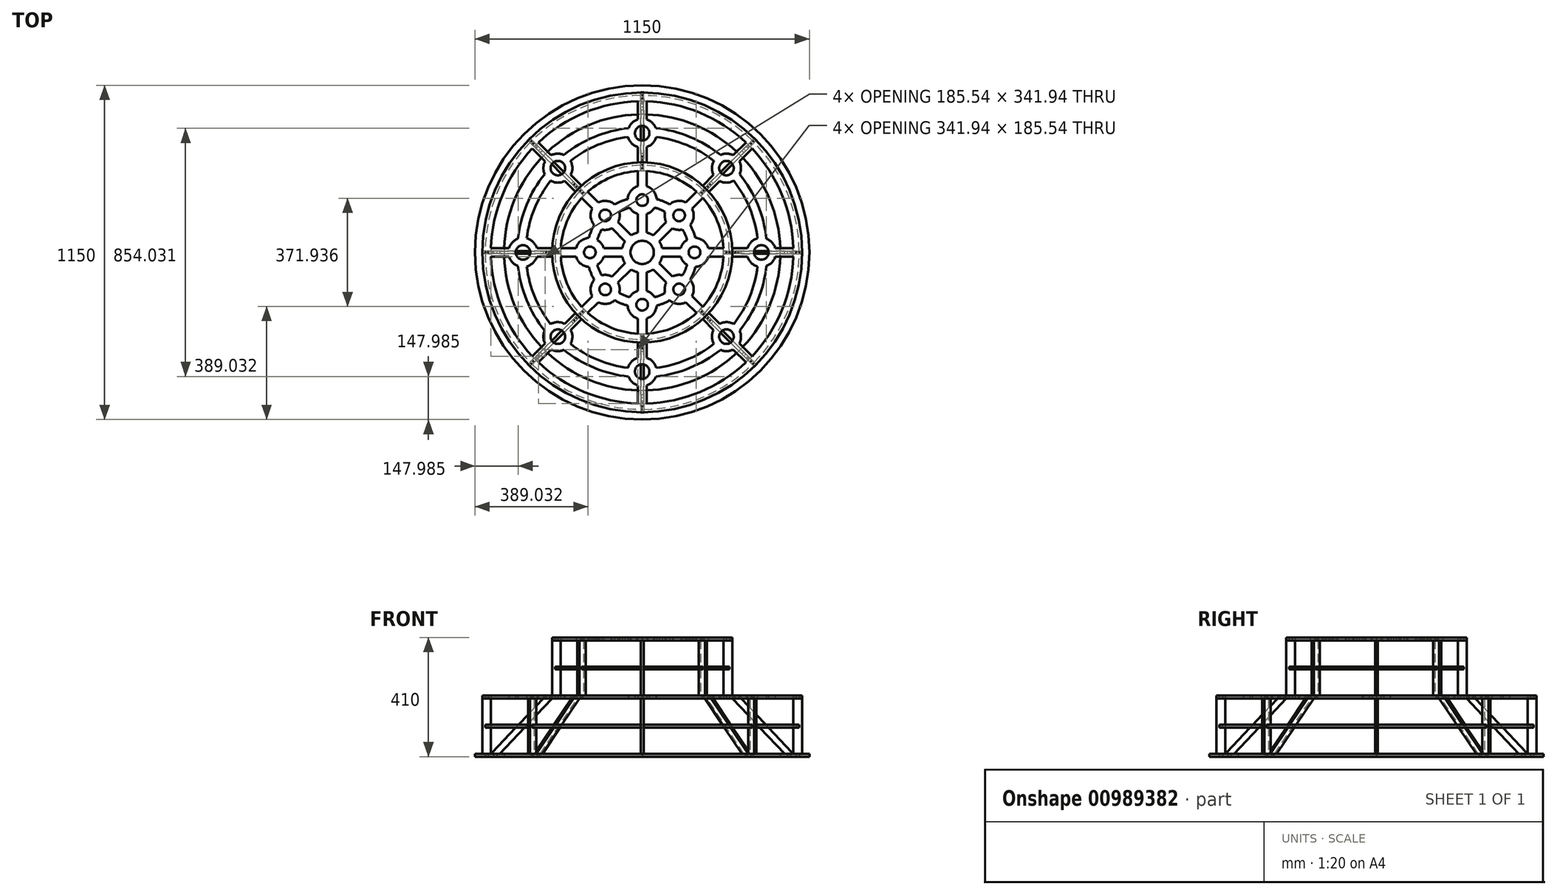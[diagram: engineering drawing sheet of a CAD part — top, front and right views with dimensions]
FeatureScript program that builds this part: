
annotation { "Feature Type Name" : "Feature", "Feature Type Description" : "" }
export const myFeature = defineFeature(function(context is Context, id is Id, definition is map)
    precondition{}
    {
        {
            var Q0;
            Q0=qCreatedBy(makeId("Top.planeOp"),FACE);
            cPlane(context, id + "F0", {"entities" : qUnion([Q0]), "cplaneType" : CPlaneType.OFFSET, "offset" : 200 * mm, "width" : 150 * mm, "height" : 150 * mm});
        }
        {
            var Q0;
            Q0=qCreatedBy(makeId("Top.planeOp"),FACE);
            cPlane(context, id + "F1", {"entities" : qUnion([Q0]), "cplaneType" : CPlaneType.OFFSET, "offset" : 200 * mm, "oppositeDirection" : true, "width" : 150 * mm, "height" : 150 * mm});
        }
        {
            var Q0;
            Q0=qCreatedBy(makeId("Top.planeOp"),FACE);
            cPlane(context, id + "F2", {"entities" : qUnion([Q0]), "cplaneType" : CPlaneType.OFFSET, "offset" : 100 * mm, "oppositeDirection" : true, "width" : 150 * mm, "height" : 150 * mm});
        }
        {
            var Q0;
            Q0=qCreatedBy(makeId("Top.planeOp"),FACE);
            cPlane(context, id + "F3", {"entities" : qUnion([Q0]), "cplaneType" : CPlaneType.OFFSET, "offset" : 100 * mm, "width" : 150 * mm, "height" : 150 * mm});
        }
        {
            var Q0;
            Q0=qCreatedBy(makeId("Top.planeOp"),FACE);
            var sketch = newSketch(context, id + "F4", { "sketchPlane" : qUnion([Q0])});
            skCircle(sketch, "E0", {"center": v(0, 0) * mm, "radius": 550 * mm});
            skArc(sketch, "E1", {"start": v(15, -519.78) * mm, "mid": v(199, -480.42) * mm, "end": v(356.94, -378.15) * mm});
            skArc(sketch, "E2", {"start": v(46.86, -427.44) * mm, "mid": v(164.55, -397.27) * mm, "end": v(269.1, -335.38) * mm});
            skArc(sketch, "E3", {"start": v(48.3, -397.07) * mm, "mid": v(153.07, -369.55) * mm, "end": v(246.62, -314.93) * mm});
            skArc(sketch, "E4", {"start": v(15, -309.64) * mm, "mid": v(118.63, -286.4) * mm, "end": v(208.34, -229.55) * mm});
            skCircle(sketch, "E5", {"center": v(0, 0) * mm, "radius": 280 * mm});
            skCircle(sketch, "E6", {"center": v(0, 0) * mm, "radius": 190 * mm, "construction": true});
            skCircle(sketch, "E7", {"center": v(0, 0) * mm, "radius": 160 * mm, "construction": true});
            skCircle(sketch, "E8", {"center": v(0, 0) * mm, "radius": 40 * mm, "construction": true});
            skCircle(sketch, "E9", {"center": v(0, 0) * mm, "radius": 70 * mm, "construction": true});
            skLineSegment(sketch, "E10", {"start": v(0, 725.48) * mm, "end": v(0, -722.46) * mm, "construction": true});
            skLineSegment(sketch, "E11", {"start": v(-695.44, 0) * mm, "end": v(901.66, 0) * mm, "construction": true});
            skArc(sketch, "E12", {"start": v(-15, -362.3) * mm, "mid": v(-36.11, -375.42) * mm, "end": v(-48.3, -397.07) * mm});
            skCircle(sketch, "E13", {"center": v(0, -410) * mm, "radius": 25 * mm});
            skLineSegment(sketch, "E14", {"start": v(15, -519.78) * mm, "end": v(15, -457.7) * mm});
            skLineSegment(sketch, "E15", {"start": v(-15, -457.7) * mm, "end": v(-15, -519.78) * mm});
            skLineSegment(sketch, "E16", {"start": v(-15, -362.3) * mm, "end": v(-15, -309.64) * mm});
            skLineSegment(sketch, "E17", {"start": v(15, -362.3) * mm, "end": v(15, -309.64) * mm});
            skArc(sketch, "E18.trimOffspring", {"start": v(-46.86, -427.44) * mm, "mid": v(-34.43, -446.26) * mm, "end": v(-15, -457.7) * mm});
            skArc(sketch, "E19.trimOffspring", {"start": v(48.3, -397.07) * mm, "mid": v(36.11, -375.42) * mm, "end": v(15, -362.3) * mm});
            skArc(sketch, "E20.trimOffspring", {"start": v(15, -457.7) * mm, "mid": v(34.43, -446.26) * mm, "end": v(46.86, -427.44) * mm});
            skArc(sketch, "E21.1.0", {"start": v(334.25, -313.03) * mm, "mid": v(339.9, -291.2) * mm, "end": v(335.38, -269.1) * mm});
            skCircle(sketch, "E21.1.1", {"center": v(289.91, -289.91) * mm, "radius": 25 * mm});
            skLineSegment(sketch, "E21.1.2", {"start": v(266.8, -245.58) * mm, "end": v(229.55, -208.34) * mm});
            skLineSegment(sketch, "E21.1.3", {"start": v(245.58, -266.8) * mm, "end": v(208.34, -229.55) * mm});
            skArc(sketch, "E21.1.4", {"start": v(245.58, -266.8) * mm, "mid": v(239.93, -291) * mm, "end": v(246.62, -314.93) * mm});
            skArc(sketch, "E21.1.5", {"start": v(269.1, -335.38) * mm, "mid": v(291.2, -339.9) * mm, "end": v(313.03, -334.25) * mm});
            skArc(sketch, "E21.1.6", {"start": v(314.93, -246.62) * mm, "mid": v(291, -239.93) * mm, "end": v(266.8, -245.58) * mm});
            skLineSegment(sketch, "E21.1.7", {"start": v(378.15, -356.94) * mm, "end": v(334.25, -313.03) * mm});
            skLineSegment(sketch, "E21.1.8", {"start": v(313.03, -334.25) * mm, "end": v(356.94, -378.15) * mm});
            skArc(sketch, "E21.2.0", {"start": v(457.7, 15) * mm, "mid": v(446.26, 34.43) * mm, "end": v(427.44, 46.86) * mm});
            skCircle(sketch, "E21.2.1", {"center": v(410, 0) * mm, "radius": 25 * mm});
            skLineSegment(sketch, "E21.2.2", {"start": v(362.3, 15) * mm, "end": v(309.64, 15) * mm});
            skLineSegment(sketch, "E21.2.3", {"start": v(362.3, -15) * mm, "end": v(309.64, -15) * mm});
            skArc(sketch, "E21.2.4", {"start": v(362.3, -15) * mm, "mid": v(375.42, -36.11) * mm, "end": v(397.07, -48.3) * mm});
            skArc(sketch, "E21.2.5", {"start": v(427.44, -46.86) * mm, "mid": v(446.26, -34.43) * mm, "end": v(457.7, -15) * mm});
            skArc(sketch, "E21.2.6", {"start": v(397.07, 48.3) * mm, "mid": v(375.42, 36.11) * mm, "end": v(362.3, 15) * mm});
            skLineSegment(sketch, "E21.2.7", {"start": v(519.78, 15) * mm, "end": v(457.7, 15) * mm});
            skLineSegment(sketch, "E21.2.8", {"start": v(457.7, -15) * mm, "end": v(519.78, -15) * mm});
            skArc(sketch, "E21.3.0", {"start": v(313.03, 334.25) * mm, "mid": v(291.2, 339.9) * mm, "end": v(269.1, 335.38) * mm});
            skCircle(sketch, "E21.3.1", {"center": v(289.91, 289.91) * mm, "radius": 25 * mm});
            skLineSegment(sketch, "E21.3.2", {"start": v(245.58, 266.8) * mm, "end": v(208.34, 229.55) * mm});
            skLineSegment(sketch, "E21.3.3", {"start": v(266.8, 245.58) * mm, "end": v(229.55, 208.34) * mm});
            skArc(sketch, "E21.3.4", {"start": v(266.8, 245.58) * mm, "mid": v(291, 239.93) * mm, "end": v(314.93, 246.62) * mm});
            skArc(sketch, "E21.3.5", {"start": v(335.38, 269.1) * mm, "mid": v(339.9, 291.2) * mm, "end": v(334.25, 313.03) * mm});
            skArc(sketch, "E21.3.6", {"start": v(246.62, 314.93) * mm, "mid": v(239.93, 291) * mm, "end": v(245.58, 266.8) * mm});
            skLineSegment(sketch, "E21.3.7", {"start": v(356.94, 378.15) * mm, "end": v(313.03, 334.25) * mm});
            skLineSegment(sketch, "E21.3.8", {"start": v(334.25, 313.03) * mm, "end": v(378.15, 356.94) * mm});
            skArc(sketch, "E21.4.0", {"start": v(-15, 457.7) * mm, "mid": v(-34.43, 446.26) * mm, "end": v(-46.86, 427.44) * mm});
            skCircle(sketch, "E21.4.1", {"center": v(0, 410) * mm, "radius": 25 * mm});
            skLineSegment(sketch, "E21.4.2", {"start": v(-15, 362.3) * mm, "end": v(-15, 309.64) * mm});
            skLineSegment(sketch, "E21.4.3", {"start": v(15, 362.3) * mm, "end": v(15, 309.64) * mm});
            skArc(sketch, "E21.4.4", {"start": v(15, 362.3) * mm, "mid": v(36.11, 375.42) * mm, "end": v(48.3, 397.07) * mm});
            skArc(sketch, "E21.4.5", {"start": v(46.86, 427.44) * mm, "mid": v(34.43, 446.26) * mm, "end": v(15, 457.7) * mm});
            skArc(sketch, "E21.4.6", {"start": v(-48.3, 397.07) * mm, "mid": v(-36.11, 375.42) * mm, "end": v(-15, 362.3) * mm});
            skLineSegment(sketch, "E21.4.7", {"start": v(-15, 519.78) * mm, "end": v(-15, 457.7) * mm});
            skLineSegment(sketch, "E21.4.8", {"start": v(15, 457.7) * mm, "end": v(15, 519.78) * mm});
            skArc(sketch, "E21.5.0", {"start": v(-334.25, 313.03) * mm, "mid": v(-339.9, 291.2) * mm, "end": v(-335.38, 269.1) * mm});
            skCircle(sketch, "E21.5.1", {"center": v(-289.91, 289.91) * mm, "radius": 25 * mm});
            skLineSegment(sketch, "E21.5.2", {"start": v(-266.8, 245.58) * mm, "end": v(-229.55, 208.34) * mm});
            skLineSegment(sketch, "E21.5.3", {"start": v(-245.58, 266.8) * mm, "end": v(-208.34, 229.55) * mm});
            skArc(sketch, "E21.5.4", {"start": v(-245.58, 266.8) * mm, "mid": v(-239.93, 291) * mm, "end": v(-246.62, 314.93) * mm});
            skArc(sketch, "E21.5.5", {"start": v(-269.1, 335.38) * mm, "mid": v(-291.2, 339.9) * mm, "end": v(-313.03, 334.25) * mm});
            skArc(sketch, "E21.5.6", {"start": v(-314.93, 246.62) * mm, "mid": v(-291, 239.93) * mm, "end": v(-266.8, 245.58) * mm});
            skLineSegment(sketch, "E21.5.7", {"start": v(-378.15, 356.94) * mm, "end": v(-334.25, 313.03) * mm});
            skLineSegment(sketch, "E21.5.8", {"start": v(-313.03, 334.25) * mm, "end": v(-356.94, 378.15) * mm});
            skArc(sketch, "E21.6.0", {"start": v(-457.7, -15) * mm, "mid": v(-446.26, -34.43) * mm, "end": v(-427.44, -46.86) * mm});
            skCircle(sketch, "E21.6.1", {"center": v(-410, 0) * mm, "radius": 25 * mm});
            skLineSegment(sketch, "E21.6.2", {"start": v(-362.3, -15) * mm, "end": v(-309.64, -15) * mm});
            skLineSegment(sketch, "E21.6.3", {"start": v(-362.3, 15) * mm, "end": v(-309.64, 15) * mm});
            skArc(sketch, "E21.6.4", {"start": v(-362.3, 15) * mm, "mid": v(-375.42, 36.11) * mm, "end": v(-397.07, 48.3) * mm});
            skArc(sketch, "E21.6.5", {"start": v(-427.44, 46.86) * mm, "mid": v(-446.26, 34.43) * mm, "end": v(-457.7, 15) * mm});
            skArc(sketch, "E21.6.6", {"start": v(-397.07, -48.3) * mm, "mid": v(-375.42, -36.11) * mm, "end": v(-362.3, -15) * mm});
            skLineSegment(sketch, "E21.6.7", {"start": v(-519.78, -15) * mm, "end": v(-457.7, -15) * mm});
            skLineSegment(sketch, "E21.6.8", {"start": v(-457.7, 15) * mm, "end": v(-519.78, 15) * mm});
            skArc(sketch, "E21.7.0", {"start": v(-313.03, -334.25) * mm, "mid": v(-291.2, -339.9) * mm, "end": v(-269.1, -335.38) * mm});
            skCircle(sketch, "E21.7.1", {"center": v(-289.91, -289.91) * mm, "radius": 25 * mm});
            skLineSegment(sketch, "E21.7.2", {"start": v(-245.58, -266.8) * mm, "end": v(-208.34, -229.55) * mm});
            skLineSegment(sketch, "E21.7.3", {"start": v(-266.8, -245.58) * mm, "end": v(-229.55, -208.34) * mm});
            skArc(sketch, "E21.7.4", {"start": v(-266.8, -245.58) * mm, "mid": v(-291, -239.93) * mm, "end": v(-314.93, -246.62) * mm});
            skArc(sketch, "E21.7.5", {"start": v(-335.38, -269.1) * mm, "mid": v(-339.9, -291.2) * mm, "end": v(-334.25, -313.03) * mm});
            skArc(sketch, "E21.7.6", {"start": v(-246.62, -314.93) * mm, "mid": v(-239.93, -291) * mm, "end": v(-245.58, -266.8) * mm});
            skLineSegment(sketch, "E21.7.7", {"start": v(-356.94, -378.15) * mm, "end": v(-313.03, -334.25) * mm});
            skLineSegment(sketch, "E21.7.8", {"start": v(-334.25, -313.03) * mm, "end": v(-378.15, -356.94) * mm});
            skArc(sketch, "E22.trimOffspring", {"start": v(-246.62, -314.93) * mm, "mid": v(-153.07, -369.55) * mm, "end": v(-48.3, -397.07) * mm});
            skArc(sketch, "E23.trimOffspring", {"start": v(-269.1, -335.38) * mm, "mid": v(-164.55, -397.27) * mm, "end": v(-46.86, -427.44) * mm});
            skArc(sketch, "E24.trimOffspring", {"start": v(-356.94, -378.15) * mm, "mid": v(-199, -480.42) * mm, "end": v(-15, -519.78) * mm});
            skArc(sketch, "E25.trimOffspring", {"start": v(-208.34, -229.55) * mm, "mid": v(-118.63, -286.4) * mm, "end": v(-15, -309.64) * mm});
            skArc(sketch, "E26.trimOffspring", {"start": v(-397.07, -48.3) * mm, "mid": v(-369.55, -153.07) * mm, "end": v(-314.93, -246.62) * mm});
            skArc(sketch, "E27.trimOffspring", {"start": v(-427.44, -46.86) * mm, "mid": v(-397.27, -164.55) * mm, "end": v(-335.38, -269.1) * mm});
            skArc(sketch, "E28.trimOffspring", {"start": v(-309.64, -15) * mm, "mid": v(-286.4, -118.63) * mm, "end": v(-229.55, -208.34) * mm});
            skArc(sketch, "E29.trimOffspring", {"start": v(-519.78, -15) * mm, "mid": v(-480.42, -199) * mm, "end": v(-378.15, -356.94) * mm});
            skArc(sketch, "E30.trimOffspring", {"start": v(-314.93, 246.62) * mm, "mid": v(-369.55, 153.07) * mm, "end": v(-397.07, 48.3) * mm});
            skArc(sketch, "E31.trimOffspring", {"start": v(-335.38, 269.1) * mm, "mid": v(-397.27, 164.55) * mm, "end": v(-427.44, 46.86) * mm});
            skArc(sketch, "E32.trimOffspring", {"start": v(-378.15, 356.94) * mm, "mid": v(-480.42, 199) * mm, "end": v(-519.78, 15) * mm});
            skArc(sketch, "E33.trimOffspring", {"start": v(-229.55, 208.34) * mm, "mid": v(-286.4, 118.63) * mm, "end": v(-309.64, 15) * mm});
            skArc(sketch, "E34.trimOffspring", {"start": v(-15, 309.64) * mm, "mid": v(-118.63, 286.4) * mm, "end": v(-208.34, 229.55) * mm});
            skArc(sketch, "E35.trimOffspring", {"start": v(-48.3, 397.07) * mm, "mid": v(-153.07, 369.55) * mm, "end": v(-246.62, 314.93) * mm});
            skArc(sketch, "E36.trimOffspring", {"start": v(-46.86, 427.44) * mm, "mid": v(-164.55, 397.27) * mm, "end": v(-269.1, 335.38) * mm});
            skArc(sketch, "E37.trimOffspring", {"start": v(-15, 519.78) * mm, "mid": v(-199, 480.42) * mm, "end": v(-356.94, 378.15) * mm});
            skArc(sketch, "E38.trimOffspring", {"start": v(269.1, 335.38) * mm, "mid": v(164.55, 397.27) * mm, "end": v(46.86, 427.44) * mm});
            skArc(sketch, "E39.trimOffspring", {"start": v(246.62, 314.93) * mm, "mid": v(153.07, 369.55) * mm, "end": v(48.3, 397.07) * mm});
            skArc(sketch, "E40.trimOffspring", {"start": v(208.34, 229.55) * mm, "mid": v(118.63, 286.4) * mm, "end": v(15, 309.64) * mm});
            skArc(sketch, "E41.trimOffspring", {"start": v(356.94, 378.15) * mm, "mid": v(199, 480.42) * mm, "end": v(15, 519.78) * mm});
            skArc(sketch, "E42.trimOffspring", {"start": v(309.64, 15) * mm, "mid": v(286.4, 118.63) * mm, "end": v(229.55, 208.34) * mm});
            skArc(sketch, "E43.trimOffspring", {"start": v(397.07, 48.3) * mm, "mid": v(369.55, 153.07) * mm, "end": v(314.93, 246.62) * mm});
            skArc(sketch, "E44.trimOffspring", {"start": v(427.44, 46.86) * mm, "mid": v(397.27, 164.55) * mm, "end": v(335.38, 269.1) * mm});
            skArc(sketch, "E45.trimOffspring", {"start": v(519.78, 15) * mm, "mid": v(480.42, 199) * mm, "end": v(378.15, 356.94) * mm});
            skArc(sketch, "E46.trimOffspring", {"start": v(335.38, -269.1) * mm, "mid": v(397.27, -164.55) * mm, "end": v(427.44, -46.86) * mm});
            skArc(sketch, "E47.trimOffspring", {"start": v(314.93, -246.62) * mm, "mid": v(369.55, -153.07) * mm, "end": v(397.07, -48.3) * mm});
            skArc(sketch, "E48.trimOffspring", {"start": v(378.15, -356.94) * mm, "mid": v(480.42, -199) * mm, "end": v(519.78, -15) * mm});
            skArc(sketch, "E49.trimOffspring", {"start": v(229.55, -208.34) * mm, "mid": v(286.4, -118.63) * mm, "end": v(309.64, -15) * mm});
            skLineSegment(sketch, "E50.bottom", {"start": v(4.9, 530) * mm, "end": v(1, 530) * mm});
            skLineSegment(sketch, "E50.top", {"start": v(4.9, 540) * mm, "end": v(1, 540) * mm});
            skLineSegment(sketch, "E50.left", {"start": v(4.9, 530) * mm, "end": v(4.9, 540) * mm});
            skLineSegment(sketch, "E50.right", {"start": v(-4.9, 530) * mm, "end": v(-4.9, 540) * mm});
            skPoint(sketch, "E50.middle", {"position": v(0, 535) * mm});
            skLineSegment(sketch, "E51", {"start": v(0, 541) * mm, "end": v(-1, 540) * mm});
            skLineSegment(sketch, "E52", {"start": v(0, 541) * mm, "end": v(1, 540) * mm});
            skLineSegment(sketch, "E53.trimOffspring", {"start": v(-1, 540) * mm, "end": v(-4.9, 540) * mm});
            skLineSegment(sketch, "E54", {"start": v(0, 529) * mm, "end": v(-1, 530) * mm});
            skLineSegment(sketch, "E55", {"start": v(0, 529) * mm, "end": v(1, 530) * mm});
            skLineSegment(sketch, "E56.trimOffspring", {"start": v(-1, 530) * mm, "end": v(-4.9, 530) * mm});
            skPoint(sketch, "E57.1.0", {"position": v(-378.3, 378.3) * mm});
            skLineSegment(sketch, "E57.1.1", {"start": v(-378.23, 371.3) * mm, "end": v(-385.3, 378.37) * mm});
            skLineSegment(sketch, "E57.1.2", {"start": v(-371.3, 378.23) * mm, "end": v(-378.37, 385.3) * mm});
            skLineSegment(sketch, "E57.1.3", {"start": v(-371.3, 378.23) * mm, "end": v(-374.06, 375.47) * mm});
            skLineSegment(sketch, "E57.1.4", {"start": v(-374.06, 374.06) * mm, "end": v(-374.06, 375.47) * mm});
            skLineSegment(sketch, "E57.1.5", {"start": v(-374.06, 374.06) * mm, "end": v(-375.47, 374.06) * mm});
            skLineSegment(sketch, "E57.1.6", {"start": v(-375.47, 374.06) * mm, "end": v(-378.23, 371.3) * mm});
            skLineSegment(sketch, "E57.1.7", {"start": v(-378.37, 385.3) * mm, "end": v(-381.13, 382.54) * mm});
            skLineSegment(sketch, "E57.1.8", {"start": v(-382.54, 381.13) * mm, "end": v(-385.3, 378.37) * mm});
            skLineSegment(sketch, "E57.1.9", {"start": v(-382.54, 382.54) * mm, "end": v(-381.13, 382.54) * mm});
            skLineSegment(sketch, "E57.1.10", {"start": v(-382.54, 382.54) * mm, "end": v(-382.54, 381.13) * mm});
            skPoint(sketch, "E57.2.0", {"position": v(-535, 0) * mm});
            skLineSegment(sketch, "E57.2.1", {"start": v(-530, -4.9) * mm, "end": v(-540, -4.9) * mm});
            skLineSegment(sketch, "E57.2.2", {"start": v(-530, 4.9) * mm, "end": v(-540, 4.9) * mm});
            skLineSegment(sketch, "E57.2.3", {"start": v(-530, 4.9) * mm, "end": v(-530, 1) * mm});
            skLineSegment(sketch, "E57.2.4", {"start": v(-529, 0) * mm, "end": v(-530, 1) * mm});
            skLineSegment(sketch, "E57.2.5", {"start": v(-529, 0) * mm, "end": v(-530, -1) * mm});
            skLineSegment(sketch, "E57.2.6", {"start": v(-530, -1) * mm, "end": v(-530, -4.9) * mm});
            skLineSegment(sketch, "E57.2.7", {"start": v(-540, 4.9) * mm, "end": v(-540, 1) * mm});
            skLineSegment(sketch, "E57.2.8", {"start": v(-540, -1) * mm, "end": v(-540, -4.9) * mm});
            skLineSegment(sketch, "E57.2.9", {"start": v(-541, 0) * mm, "end": v(-540, 1) * mm});
            skLineSegment(sketch, "E57.2.10", {"start": v(-541, 0) * mm, "end": v(-540, -1) * mm});
            skPoint(sketch, "E57.3.0", {"position": v(-378.3, -378.3) * mm});
            skLineSegment(sketch, "E57.3.1", {"start": v(-371.3, -378.23) * mm, "end": v(-378.37, -385.3) * mm});
            skLineSegment(sketch, "E57.3.2", {"start": v(-378.23, -371.3) * mm, "end": v(-385.3, -378.37) * mm});
            skLineSegment(sketch, "E57.3.3", {"start": v(-378.23, -371.3) * mm, "end": v(-375.47, -374.06) * mm});
            skLineSegment(sketch, "E57.3.4", {"start": v(-374.06, -374.06) * mm, "end": v(-375.47, -374.06) * mm});
            skLineSegment(sketch, "E57.3.5", {"start": v(-374.06, -374.06) * mm, "end": v(-374.06, -375.47) * mm});
            skLineSegment(sketch, "E57.3.6", {"start": v(-374.06, -375.47) * mm, "end": v(-371.3, -378.23) * mm});
            skLineSegment(sketch, "E57.3.7", {"start": v(-385.3, -378.37) * mm, "end": v(-382.54, -381.13) * mm});
            skLineSegment(sketch, "E57.3.8", {"start": v(-381.13, -382.54) * mm, "end": v(-378.37, -385.3) * mm});
            skLineSegment(sketch, "E57.3.9", {"start": v(-382.54, -382.54) * mm, "end": v(-382.54, -381.13) * mm});
            skLineSegment(sketch, "E57.3.10", {"start": v(-382.54, -382.54) * mm, "end": v(-381.13, -382.54) * mm});
            skPoint(sketch, "E57.4.0", {"position": v(0, -535) * mm});
            skLineSegment(sketch, "E57.4.1", {"start": v(4.9, -530) * mm, "end": v(4.9, -540) * mm});
            skLineSegment(sketch, "E57.4.2", {"start": v(-4.9, -530) * mm, "end": v(-4.9, -540) * mm});
            skLineSegment(sketch, "E57.4.3", {"start": v(-4.9, -530) * mm, "end": v(-1, -530) * mm});
            skLineSegment(sketch, "E57.4.4", {"start": v(0, -529) * mm, "end": v(-1, -530) * mm});
            skLineSegment(sketch, "E57.4.5", {"start": v(0, -529) * mm, "end": v(1, -530) * mm});
            skLineSegment(sketch, "E57.4.6", {"start": v(1, -530) * mm, "end": v(4.9, -530) * mm});
            skLineSegment(sketch, "E57.4.7", {"start": v(-4.9, -540) * mm, "end": v(-1, -540) * mm});
            skLineSegment(sketch, "E57.4.8", {"start": v(1, -540) * mm, "end": v(4.9, -540) * mm});
            skLineSegment(sketch, "E57.4.9", {"start": v(0, -541) * mm, "end": v(-1, -540) * mm});
            skLineSegment(sketch, "E57.4.10", {"start": v(0, -541) * mm, "end": v(1, -540) * mm});
            skPoint(sketch, "E57.5.0", {"position": v(378.3, -378.3) * mm});
            skLineSegment(sketch, "E57.5.1", {"start": v(378.23, -371.3) * mm, "end": v(385.3, -378.37) * mm});
            skLineSegment(sketch, "E57.5.2", {"start": v(371.3, -378.23) * mm, "end": v(378.37, -385.3) * mm});
            skLineSegment(sketch, "E57.5.3", {"start": v(371.3, -378.23) * mm, "end": v(374.06, -375.47) * mm});
            skLineSegment(sketch, "E57.5.4", {"start": v(374.06, -374.06) * mm, "end": v(374.06, -375.47) * mm});
            skLineSegment(sketch, "E57.5.5", {"start": v(374.06, -374.06) * mm, "end": v(375.47, -374.06) * mm});
            skLineSegment(sketch, "E57.5.6", {"start": v(375.47, -374.06) * mm, "end": v(378.23, -371.3) * mm});
            skLineSegment(sketch, "E57.5.7", {"start": v(378.37, -385.3) * mm, "end": v(381.13, -382.54) * mm});
            skLineSegment(sketch, "E57.5.8", {"start": v(382.54, -381.13) * mm, "end": v(385.3, -378.37) * mm});
            skLineSegment(sketch, "E57.5.9", {"start": v(382.54, -382.54) * mm, "end": v(381.13, -382.54) * mm});
            skLineSegment(sketch, "E57.5.10", {"start": v(382.54, -382.54) * mm, "end": v(382.54, -381.13) * mm});
            skPoint(sketch, "E57.6.0", {"position": v(535, 0) * mm});
            skLineSegment(sketch, "E57.6.1", {"start": v(530, 4.9) * mm, "end": v(540, 4.9) * mm});
            skLineSegment(sketch, "E57.6.2", {"start": v(530, -4.9) * mm, "end": v(540, -4.9) * mm});
            skLineSegment(sketch, "E57.6.3", {"start": v(530, -4.9) * mm, "end": v(530, -1) * mm});
            skLineSegment(sketch, "E57.6.4", {"start": v(529, 0) * mm, "end": v(530, -1) * mm});
            skLineSegment(sketch, "E57.6.5", {"start": v(529, 0) * mm, "end": v(530, 1) * mm});
            skLineSegment(sketch, "E57.6.6", {"start": v(530, 1) * mm, "end": v(530, 4.9) * mm});
            skLineSegment(sketch, "E57.6.7", {"start": v(540, -4.9) * mm, "end": v(540, -1) * mm});
            skLineSegment(sketch, "E57.6.8", {"start": v(540, 1) * mm, "end": v(540, 4.9) * mm});
            skLineSegment(sketch, "E57.6.9", {"start": v(541, 0) * mm, "end": v(540, -1) * mm});
            skLineSegment(sketch, "E57.6.10", {"start": v(541, 0) * mm, "end": v(540, 1) * mm});
            skPoint(sketch, "E57.7.0", {"position": v(378.3, 378.3) * mm});
            skLineSegment(sketch, "E57.7.1", {"start": v(371.3, 378.23) * mm, "end": v(378.37, 385.3) * mm});
            skLineSegment(sketch, "E57.7.2", {"start": v(378.23, 371.3) * mm, "end": v(385.3, 378.37) * mm});
            skLineSegment(sketch, "E57.7.3", {"start": v(378.23, 371.3) * mm, "end": v(375.47, 374.06) * mm});
            skLineSegment(sketch, "E57.7.4", {"start": v(374.06, 374.06) * mm, "end": v(375.47, 374.06) * mm});
            skLineSegment(sketch, "E57.7.5", {"start": v(374.06, 374.06) * mm, "end": v(374.06, 375.47) * mm});
            skLineSegment(sketch, "E57.7.6", {"start": v(374.06, 375.47) * mm, "end": v(371.3, 378.23) * mm});
            skLineSegment(sketch, "E57.7.7", {"start": v(385.3, 378.37) * mm, "end": v(382.54, 381.13) * mm});
            skLineSegment(sketch, "E57.7.8", {"start": v(381.13, 382.54) * mm, "end": v(378.37, 385.3) * mm});
            skLineSegment(sketch, "E57.7.9", {"start": v(382.54, 382.54) * mm, "end": v(382.54, 381.13) * mm});
            skLineSegment(sketch, "E57.7.10", {"start": v(382.54, 382.54) * mm, "end": v(381.13, 382.54) * mm});
            skLineSegment(sketch, "E58.bottom", {"start": v(4.9, 290) * mm, "end": v(1, 290) * mm});
            skLineSegment(sketch, "E58.top", {"start": v(4.9, 300) * mm, "end": v(1, 300) * mm});
            skLineSegment(sketch, "E58.left", {"start": v(4.9, 290) * mm, "end": v(4.9, 300) * mm});
            skLineSegment(sketch, "E58.right", {"start": v(-4.9, 290) * mm, "end": v(-4.9, 300) * mm});
            skPoint(sketch, "E58.middle", {"position": v(0, 295) * mm});
            skLineSegment(sketch, "E59", {"start": v(0, 301) * mm, "end": v(-1, 300) * mm});
            skLineSegment(sketch, "E60", {"start": v(0, 301) * mm, "end": v(1, 300) * mm});
            skLineSegment(sketch, "E61.trimOffspring", {"start": v(-1, 300) * mm, "end": v(-4.9, 300) * mm});
            skLineSegment(sketch, "E62", {"start": v(0, 289) * mm, "end": v(-1, 290) * mm});
            skLineSegment(sketch, "E63", {"start": v(0, 289) * mm, "end": v(1, 290) * mm});
            skLineSegment(sketch, "E64.trimOffspring", {"start": v(-1, 290) * mm, "end": v(-4.9, 290) * mm});
            skLineSegment(sketch, "E65.1.0", {"start": v(-201.6, 208.53) * mm, "end": v(-208.67, 215.6) * mm});
            skPoint(sketch, "E65.1.1", {"position": v(-208.6, 208.6) * mm});
            skLineSegment(sketch, "E65.1.2", {"start": v(-208.53, 201.6) * mm, "end": v(-215.6, 208.67) * mm});
            skLineSegment(sketch, "E65.1.3", {"start": v(-205.77, 204.35) * mm, "end": v(-208.53, 201.6) * mm});
            skLineSegment(sketch, "E65.1.4", {"start": v(-208.67, 215.6) * mm, "end": v(-211.42, 212.84) * mm});
            skLineSegment(sketch, "E65.1.5", {"start": v(-201.6, 208.53) * mm, "end": v(-204.35, 205.77) * mm});
            skLineSegment(sketch, "E65.1.6", {"start": v(-212.84, 211.42) * mm, "end": v(-215.6, 208.67) * mm});
            skLineSegment(sketch, "E65.1.7", {"start": v(-204.35, 204.35) * mm, "end": v(-205.77, 204.35) * mm});
            skLineSegment(sketch, "E65.1.8", {"start": v(-212.84, 212.84) * mm, "end": v(-211.42, 212.84) * mm});
            skLineSegment(sketch, "E65.1.9", {"start": v(-212.84, 212.84) * mm, "end": v(-212.84, 211.42) * mm});
            skLineSegment(sketch, "E65.1.10", {"start": v(-204.35, 204.35) * mm, "end": v(-204.35, 205.77) * mm});
            skLineSegment(sketch, "E65.2.0", {"start": v(-290, 4.9) * mm, "end": v(-300, 4.9) * mm});
            skPoint(sketch, "E65.2.1", {"position": v(-295, 0) * mm});
            skLineSegment(sketch, "E65.2.2", {"start": v(-290, -4.9) * mm, "end": v(-300, -4.9) * mm});
            skLineSegment(sketch, "E65.2.3", {"start": v(-290, -1) * mm, "end": v(-290, -4.9) * mm});
            skLineSegment(sketch, "E65.2.4", {"start": v(-300, 4.9) * mm, "end": v(-300, 1) * mm});
            skLineSegment(sketch, "E65.2.5", {"start": v(-290, 4.9) * mm, "end": v(-290, 1) * mm});
            skLineSegment(sketch, "E65.2.6", {"start": v(-300, -1) * mm, "end": v(-300, -4.9) * mm});
            skLineSegment(sketch, "E65.2.7", {"start": v(-289, 0) * mm, "end": v(-290, -1) * mm});
            skLineSegment(sketch, "E65.2.8", {"start": v(-301, 0) * mm, "end": v(-300, 1) * mm});
            skLineSegment(sketch, "E65.2.9", {"start": v(-301, 0) * mm, "end": v(-300, -1) * mm});
            skLineSegment(sketch, "E65.2.10", {"start": v(-289, 0) * mm, "end": v(-290, 1) * mm});
            skLineSegment(sketch, "E65.3.0", {"start": v(-208.53, -201.6) * mm, "end": v(-215.6, -208.67) * mm});
            skPoint(sketch, "E65.3.1", {"position": v(-208.6, -208.6) * mm});
            skLineSegment(sketch, "E65.3.2", {"start": v(-201.6, -208.53) * mm, "end": v(-208.67, -215.6) * mm});
            skLineSegment(sketch, "E65.3.3", {"start": v(-204.35, -205.77) * mm, "end": v(-201.6, -208.53) * mm});
            skLineSegment(sketch, "E65.3.4", {"start": v(-215.6, -208.67) * mm, "end": v(-212.84, -211.42) * mm});
            skLineSegment(sketch, "E65.3.5", {"start": v(-208.53, -201.6) * mm, "end": v(-205.77, -204.35) * mm});
            skLineSegment(sketch, "E65.3.6", {"start": v(-211.42, -212.84) * mm, "end": v(-208.67, -215.6) * mm});
            skLineSegment(sketch, "E65.3.7", {"start": v(-204.35, -204.35) * mm, "end": v(-204.35, -205.77) * mm});
            skLineSegment(sketch, "E65.3.8", {"start": v(-212.84, -212.84) * mm, "end": v(-212.84, -211.42) * mm});
            skLineSegment(sketch, "E65.3.9", {"start": v(-212.84, -212.84) * mm, "end": v(-211.42, -212.84) * mm});
            skLineSegment(sketch, "E65.3.10", {"start": v(-204.35, -204.35) * mm, "end": v(-205.77, -204.35) * mm});
            skLineSegment(sketch, "E65.4.0", {"start": v(-4.9, -290) * mm, "end": v(-4.9, -300) * mm});
            skPoint(sketch, "E65.4.1", {"position": v(0, -295) * mm});
            skLineSegment(sketch, "E65.4.2", {"start": v(4.9, -290) * mm, "end": v(4.9, -300) * mm});
            skLineSegment(sketch, "E65.4.3", {"start": v(1, -290) * mm, "end": v(4.9, -290) * mm});
            skLineSegment(sketch, "E65.4.4", {"start": v(-4.9, -300) * mm, "end": v(-1, -300) * mm});
            skLineSegment(sketch, "E65.4.5", {"start": v(-4.9, -290) * mm, "end": v(-1, -290) * mm});
            skLineSegment(sketch, "E65.4.6", {"start": v(1, -300) * mm, "end": v(4.9, -300) * mm});
            skLineSegment(sketch, "E65.4.7", {"start": v(0, -289) * mm, "end": v(1, -290) * mm});
            skLineSegment(sketch, "E65.4.8", {"start": v(0, -301) * mm, "end": v(-1, -300) * mm});
            skLineSegment(sketch, "E65.4.9", {"start": v(0, -301) * mm, "end": v(1, -300) * mm});
            skLineSegment(sketch, "E65.4.10", {"start": v(0, -289) * mm, "end": v(-1, -290) * mm});
            skLineSegment(sketch, "E65.5.0", {"start": v(201.6, -208.53) * mm, "end": v(208.67, -215.6) * mm});
            skPoint(sketch, "E65.5.1", {"position": v(208.6, -208.6) * mm});
            skLineSegment(sketch, "E65.5.2", {"start": v(208.53, -201.6) * mm, "end": v(215.6, -208.67) * mm});
            skLineSegment(sketch, "E65.5.3", {"start": v(205.77, -204.35) * mm, "end": v(208.53, -201.6) * mm});
            skLineSegment(sketch, "E65.5.4", {"start": v(208.67, -215.6) * mm, "end": v(211.42, -212.84) * mm});
            skLineSegment(sketch, "E65.5.5", {"start": v(201.6, -208.53) * mm, "end": v(204.35, -205.77) * mm});
            skLineSegment(sketch, "E65.5.6", {"start": v(212.84, -211.42) * mm, "end": v(215.6, -208.67) * mm});
            skLineSegment(sketch, "E65.5.7", {"start": v(204.35, -204.35) * mm, "end": v(205.77, -204.35) * mm});
            skLineSegment(sketch, "E65.5.8", {"start": v(212.84, -212.84) * mm, "end": v(211.42, -212.84) * mm});
            skLineSegment(sketch, "E65.5.9", {"start": v(212.84, -212.84) * mm, "end": v(212.84, -211.42) * mm});
            skLineSegment(sketch, "E65.5.10", {"start": v(204.35, -204.35) * mm, "end": v(204.35, -205.77) * mm});
            skLineSegment(sketch, "E65.6.0", {"start": v(290, -4.9) * mm, "end": v(300, -4.9) * mm});
            skPoint(sketch, "E65.6.1", {"position": v(295, 0) * mm});
            skLineSegment(sketch, "E65.6.2", {"start": v(290, 4.9) * mm, "end": v(300, 4.9) * mm});
            skLineSegment(sketch, "E65.6.3", {"start": v(290, 1) * mm, "end": v(290, 4.9) * mm});
            skLineSegment(sketch, "E65.6.4", {"start": v(300, -4.9) * mm, "end": v(300, -1) * mm});
            skLineSegment(sketch, "E65.6.5", {"start": v(290, -4.9) * mm, "end": v(290, -1) * mm});
            skLineSegment(sketch, "E65.6.6", {"start": v(300, 1) * mm, "end": v(300, 4.9) * mm});
            skLineSegment(sketch, "E65.6.7", {"start": v(289, 0) * mm, "end": v(290, 1) * mm});
            skLineSegment(sketch, "E65.6.8", {"start": v(301, 0) * mm, "end": v(300, -1) * mm});
            skLineSegment(sketch, "E65.6.9", {"start": v(301, 0) * mm, "end": v(300, 1) * mm});
            skLineSegment(sketch, "E65.6.10", {"start": v(289, 0) * mm, "end": v(290, -1) * mm});
            skLineSegment(sketch, "E65.7.0", {"start": v(208.53, 201.6) * mm, "end": v(215.6, 208.67) * mm});
            skPoint(sketch, "E65.7.1", {"position": v(208.6, 208.6) * mm});
            skLineSegment(sketch, "E65.7.2", {"start": v(201.6, 208.53) * mm, "end": v(208.67, 215.6) * mm});
            skLineSegment(sketch, "E65.7.3", {"start": v(204.35, 205.77) * mm, "end": v(201.6, 208.53) * mm});
            skLineSegment(sketch, "E65.7.4", {"start": v(215.6, 208.67) * mm, "end": v(212.84, 211.42) * mm});
            skLineSegment(sketch, "E65.7.5", {"start": v(208.53, 201.6) * mm, "end": v(205.77, 204.35) * mm});
            skLineSegment(sketch, "E65.7.6", {"start": v(211.42, 212.84) * mm, "end": v(208.67, 215.6) * mm});
            skLineSegment(sketch, "E65.7.7", {"start": v(204.35, 204.35) * mm, "end": v(204.35, 205.77) * mm});
            skLineSegment(sketch, "E65.7.8", {"start": v(212.84, 212.84) * mm, "end": v(212.84, 211.42) * mm});
            skLineSegment(sketch, "E65.7.9", {"start": v(212.84, 212.84) * mm, "end": v(211.42, 212.84) * mm});
            skLineSegment(sketch, "E65.7.10", {"start": v(204.35, 204.35) * mm, "end": v(205.77, 204.35) * mm});
            skLineSegment(sketch, "E66.bottom", {"start": v(4.9, 320) * mm, "end": v(1, 320) * mm});
            skLineSegment(sketch, "E66.top", {"start": v(4.9, 330) * mm, "end": v(1, 330) * mm});
            skLineSegment(sketch, "E66.left", {"start": v(4.9, 320) * mm, "end": v(4.9, 330) * mm});
            skLineSegment(sketch, "E66.right", {"start": v(-4.9, 320) * mm, "end": v(-4.9, 330) * mm});
            skPoint(sketch, "E66.middle", {"position": v(0, 325) * mm});
            skLineSegment(sketch, "E67", {"start": v(0, 331) * mm, "end": v(-1, 330) * mm});
            skLineSegment(sketch, "E68", {"start": v(0, 331) * mm, "end": v(1, 330) * mm});
            skLineSegment(sketch, "E69.trimOffspring", {"start": v(-1, 330) * mm, "end": v(-4.9, 330) * mm});
            skLineSegment(sketch, "E70", {"start": v(0, 319) * mm, "end": v(-1, 320) * mm});
            skLineSegment(sketch, "E71", {"start": v(0, 319) * mm, "end": v(1, 320) * mm});
            skLineSegment(sketch, "E72.trimOffspring", {"start": v(-1, 320) * mm, "end": v(-4.9, 320) * mm});
            skLineSegment(sketch, "E73.1.0", {"start": v(-222.8, 229.74) * mm, "end": v(-225.57, 226.98) * mm});
            skLineSegment(sketch, "E73.1.1", {"start": v(-229.74, 222.8) * mm, "end": v(-236.81, 229.88) * mm});
            skLineSegment(sketch, "E73.1.2", {"start": v(-222.8, 229.74) * mm, "end": v(-229.88, 236.81) * mm});
            skLineSegment(sketch, "E73.1.3", {"start": v(-229.88, 236.81) * mm, "end": v(-232.64, 234.05) * mm});
            skLineSegment(sketch, "E73.1.4", {"start": v(-234.05, 232.64) * mm, "end": v(-236.81, 229.88) * mm});
            skLineSegment(sketch, "E73.1.5", {"start": v(-226.98, 225.57) * mm, "end": v(-229.74, 222.8) * mm});
            skPoint(sketch, "E73.1.6", {"position": v(-229.8, 229.8) * mm});
            skLineSegment(sketch, "E73.1.7", {"start": v(-225.57, 225.57) * mm, "end": v(-225.57, 226.98) * mm});
            skLineSegment(sketch, "E73.1.8", {"start": v(-225.57, 225.57) * mm, "end": v(-226.98, 225.57) * mm});
            skLineSegment(sketch, "E73.1.9", {"start": v(-234.05, 234.05) * mm, "end": v(-234.05, 232.64) * mm});
            skLineSegment(sketch, "E73.1.10", {"start": v(-234.05, 234.05) * mm, "end": v(-232.64, 234.05) * mm});
            skLineSegment(sketch, "E73.2.0", {"start": v(-320, 4.9) * mm, "end": v(-320, 1) * mm});
            skLineSegment(sketch, "E73.2.1", {"start": v(-320, -4.9) * mm, "end": v(-330, -4.9) * mm});
            skLineSegment(sketch, "E73.2.2", {"start": v(-320, 4.9) * mm, "end": v(-330, 4.9) * mm});
            skLineSegment(sketch, "E73.2.3", {"start": v(-330, 4.9) * mm, "end": v(-330, 1) * mm});
            skLineSegment(sketch, "E73.2.4", {"start": v(-330, -1) * mm, "end": v(-330, -4.9) * mm});
            skLineSegment(sketch, "E73.2.5", {"start": v(-320, -1) * mm, "end": v(-320, -4.9) * mm});
            skPoint(sketch, "E73.2.6", {"position": v(-325, 0) * mm});
            skLineSegment(sketch, "E73.2.7", {"start": v(-319, 0) * mm, "end": v(-320, 1) * mm});
            skLineSegment(sketch, "E73.2.8", {"start": v(-319, 0) * mm, "end": v(-320, -1) * mm});
            skLineSegment(sketch, "E73.2.9", {"start": v(-331, 0) * mm, "end": v(-330, -1) * mm});
            skLineSegment(sketch, "E73.2.10", {"start": v(-331, 0) * mm, "end": v(-330, 1) * mm});
            skLineSegment(sketch, "E73.3.0", {"start": v(-229.74, -222.8) * mm, "end": v(-226.98, -225.57) * mm});
            skLineSegment(sketch, "E73.3.1", {"start": v(-222.8, -229.74) * mm, "end": v(-229.88, -236.81) * mm});
            skLineSegment(sketch, "E73.3.2", {"start": v(-229.74, -222.8) * mm, "end": v(-236.81, -229.88) * mm});
            skLineSegment(sketch, "E73.3.3", {"start": v(-236.81, -229.88) * mm, "end": v(-234.05, -232.64) * mm});
            skLineSegment(sketch, "E73.3.4", {"start": v(-232.64, -234.05) * mm, "end": v(-229.88, -236.81) * mm});
            skLineSegment(sketch, "E73.3.5", {"start": v(-225.57, -226.98) * mm, "end": v(-222.8, -229.74) * mm});
            skPoint(sketch, "E73.3.6", {"position": v(-229.8, -229.8) * mm});
            skLineSegment(sketch, "E73.3.7", {"start": v(-225.57, -225.57) * mm, "end": v(-226.98, -225.57) * mm});
            skLineSegment(sketch, "E73.3.8", {"start": v(-225.57, -225.57) * mm, "end": v(-225.57, -226.98) * mm});
            skLineSegment(sketch, "E73.3.9", {"start": v(-234.05, -234.05) * mm, "end": v(-232.64, -234.05) * mm});
            skLineSegment(sketch, "E73.3.10", {"start": v(-234.05, -234.05) * mm, "end": v(-234.05, -232.64) * mm});
            skLineSegment(sketch, "E73.4.0", {"start": v(-4.9, -320) * mm, "end": v(-1, -320) * mm});
            skLineSegment(sketch, "E73.4.1", {"start": v(4.9, -320) * mm, "end": v(4.9, -330) * mm});
            skLineSegment(sketch, "E73.4.2", {"start": v(-4.9, -320) * mm, "end": v(-4.9, -330) * mm});
            skLineSegment(sketch, "E73.4.3", {"start": v(-4.9, -330) * mm, "end": v(-1, -330) * mm});
            skLineSegment(sketch, "E73.4.4", {"start": v(1, -330) * mm, "end": v(4.9, -330) * mm});
            skLineSegment(sketch, "E73.4.5", {"start": v(1, -320) * mm, "end": v(4.9, -320) * mm});
            skPoint(sketch, "E73.4.6", {"position": v(0, -325) * mm});
            skLineSegment(sketch, "E73.4.7", {"start": v(0, -319) * mm, "end": v(-1, -320) * mm});
            skLineSegment(sketch, "E73.4.8", {"start": v(0, -319) * mm, "end": v(1, -320) * mm});
            skLineSegment(sketch, "E73.4.9", {"start": v(0, -331) * mm, "end": v(1, -330) * mm});
            skLineSegment(sketch, "E73.4.10", {"start": v(0, -331) * mm, "end": v(-1, -330) * mm});
            skLineSegment(sketch, "E73.5.0", {"start": v(222.8, -229.74) * mm, "end": v(225.57, -226.98) * mm});
            skLineSegment(sketch, "E73.5.1", {"start": v(229.74, -222.8) * mm, "end": v(236.81, -229.88) * mm});
            skLineSegment(sketch, "E73.5.2", {"start": v(222.8, -229.74) * mm, "end": v(229.88, -236.81) * mm});
            skLineSegment(sketch, "E73.5.3", {"start": v(229.88, -236.81) * mm, "end": v(232.64, -234.05) * mm});
            skLineSegment(sketch, "E73.5.4", {"start": v(234.05, -232.64) * mm, "end": v(236.81, -229.88) * mm});
            skLineSegment(sketch, "E73.5.5", {"start": v(226.98, -225.57) * mm, "end": v(229.74, -222.8) * mm});
            skPoint(sketch, "E73.5.6", {"position": v(229.8, -229.8) * mm});
            skLineSegment(sketch, "E73.5.7", {"start": v(225.57, -225.57) * mm, "end": v(225.57, -226.98) * mm});
            skLineSegment(sketch, "E73.5.8", {"start": v(225.57, -225.57) * mm, "end": v(226.98, -225.57) * mm});
            skLineSegment(sketch, "E73.5.9", {"start": v(234.05, -234.05) * mm, "end": v(234.05, -232.64) * mm});
            skLineSegment(sketch, "E73.5.10", {"start": v(234.05, -234.05) * mm, "end": v(232.64, -234.05) * mm});
            skLineSegment(sketch, "E73.6.0", {"start": v(320, -4.9) * mm, "end": v(320, -1) * mm});
            skLineSegment(sketch, "E73.6.1", {"start": v(320, 4.9) * mm, "end": v(330, 4.9) * mm});
            skLineSegment(sketch, "E73.6.2", {"start": v(320, -4.9) * mm, "end": v(330, -4.9) * mm});
            skLineSegment(sketch, "E73.6.3", {"start": v(330, -4.9) * mm, "end": v(330, -1) * mm});
            skLineSegment(sketch, "E73.6.4", {"start": v(330, 1) * mm, "end": v(330, 4.9) * mm});
            skLineSegment(sketch, "E73.6.5", {"start": v(320, 1) * mm, "end": v(320, 4.9) * mm});
            skPoint(sketch, "E73.6.6", {"position": v(325, 0) * mm});
            skLineSegment(sketch, "E73.6.7", {"start": v(319, 0) * mm, "end": v(320, -1) * mm});
            skLineSegment(sketch, "E73.6.8", {"start": v(319, 0) * mm, "end": v(320, 1) * mm});
            skLineSegment(sketch, "E73.6.9", {"start": v(331, 0) * mm, "end": v(330, 1) * mm});
            skLineSegment(sketch, "E73.6.10", {"start": v(331, 0) * mm, "end": v(330, -1) * mm});
            skLineSegment(sketch, "E73.7.0", {"start": v(229.74, 222.8) * mm, "end": v(226.98, 225.57) * mm});
            skLineSegment(sketch, "E73.7.1", {"start": v(222.8, 229.74) * mm, "end": v(229.88, 236.81) * mm});
            skLineSegment(sketch, "E73.7.2", {"start": v(229.74, 222.8) * mm, "end": v(236.81, 229.88) * mm});
            skLineSegment(sketch, "E73.7.3", {"start": v(236.81, 229.88) * mm, "end": v(234.05, 232.64) * mm});
            skLineSegment(sketch, "E73.7.4", {"start": v(232.64, 234.05) * mm, "end": v(229.88, 236.81) * mm});
            skLineSegment(sketch, "E73.7.5", {"start": v(225.57, 226.98) * mm, "end": v(222.8, 229.74) * mm});
            skPoint(sketch, "E73.7.6", {"position": v(229.8, 229.8) * mm});
            skLineSegment(sketch, "E73.7.7", {"start": v(225.57, 225.57) * mm, "end": v(226.98, 225.57) * mm});
            skLineSegment(sketch, "E73.7.8", {"start": v(225.57, 225.57) * mm, "end": v(225.57, 226.98) * mm});
            skLineSegment(sketch, "E73.7.9", {"start": v(234.05, 234.05) * mm, "end": v(232.64, 234.05) * mm});
            skLineSegment(sketch, "E73.7.10", {"start": v(234.05, 234.05) * mm, "end": v(234.05, 232.64) * mm});
            skSolve(sketch);
        }
        {
            var Q0;
            Q0=qSketchRegion(id+"F4",true);
            extrude(context, id + "F5", {"entities" : qUnion([Q0]), "depth" : 10 * mm, "offsetDistance" : 25 * mm});
        }
        {
            var Q0;
            Q0=qCreatedBy(id+"F0.planeOp",FACE);
            var sketch = newSketch(context, id + "F6", { "sketchPlane" : qUnion([Q0])});
            skArc(sketch, "E74.0", {"start": v(42.8, -154.17) * mm, "mid": v(61.23, -147.82) * mm, "end": v(78.74, -139.28) * mm});
            skArc(sketch, "E75.0", {"start": v(49.89, -183.33) * mm, "mid": v(72.7, -175.54) * mm, "end": v(94.36, -164.91) * mm});
            skArc(sketch, "E76.0", {"start": v(15, -279.6) * mm, "mid": v(107.15, -258.69) * mm, "end": v(187.1, -208.31) * mm});
            skArc(sketch, "E77.0", {"start": v(15, -68.37) * mm, "mid": v(26.79, -64.67) * mm, "end": v(37.74, -58.95) * mm});
            skCircle(sketch, "E78.0", {"center": v(0, 0) * mm, "radius": 40 * mm});
            skPoint(sketch, "E79.0", {"position": v(15, 309.64) * mm});
            skCircle(sketch, "E80", {"center": v(0, 0) * mm, "radius": 310 * mm});
            skArc(sketch, "E81", {"start": v(-15, -132.3) * mm, "mid": v(-30.9, -140.7) * mm, "end": v(-42.8, -154.17) * mm});
            skCircle(sketch, "E82", {"center": v(0, -180) * mm, "radius": 20 * mm});
            skLineSegment(sketch, "E83", {"start": v(-15, -68.37) * mm, "end": v(-15, -132.3) * mm});
            skLineSegment(sketch, "E84", {"start": v(15, -68.37) * mm, "end": v(15, -132.3) * mm});
            skLineSegment(sketch, "E85", {"start": v(-15, -227.7) * mm, "end": v(-15, -279.6) * mm});
            skLineSegment(sketch, "E86", {"start": v(15, -227.7) * mm, "end": v(15, -279.6) * mm});
            skArc(sketch, "E87.trimOffspring", {"start": v(42.8, -154.17) * mm, "mid": v(30.9, -140.7) * mm, "end": v(15, -132.3) * mm});
            skArc(sketch, "E88.trimOffspring", {"start": v(15, -227.7) * mm, "mid": v(39.3, -210.9) * mm, "end": v(49.89, -183.33) * mm});
            skArc(sketch, "E89.trimOffspring", {"start": v(-49.89, -183.33) * mm, "mid": v(-39.3, -210.9) * mm, "end": v(-15, -227.7) * mm});
            skLineSegment(sketch, "E90.1.0", {"start": v(58.95, -37.74) * mm, "end": v(104.16, -82.95) * mm});
            skLineSegment(sketch, "E90.1.1", {"start": v(37.74, -58.95) * mm, "end": v(82.95, -104.16) * mm});
            skArc(sketch, "E90.1.2", {"start": v(82.95, -104.16) * mm, "mid": v(77.63, -121.34) * mm, "end": v(78.74, -139.28) * mm});
            skCircle(sketch, "E90.1.3", {"center": v(127.28, -127.28) * mm, "radius": 20 * mm});
            skArc(sketch, "E90.1.4", {"start": v(94.36, -164.91) * mm, "mid": v(121.34, -176.93) * mm, "end": v(150.4, -171.61) * mm});
            skArc(sketch, "E90.1.5", {"start": v(171.61, -150.4) * mm, "mid": v(176.93, -121.34) * mm, "end": v(164.91, -94.36) * mm});
            skArc(sketch, "E90.1.6", {"start": v(139.28, -78.74) * mm, "mid": v(121.34, -77.63) * mm, "end": v(104.16, -82.95) * mm});
            skLineSegment(sketch, "E90.1.7", {"start": v(171.61, -150.4) * mm, "end": v(208.31, -187.1) * mm});
            skLineSegment(sketch, "E90.1.8", {"start": v(150.4, -171.61) * mm, "end": v(187.1, -208.31) * mm});
            skLineSegment(sketch, "E90.2.0", {"start": v(68.37, 15) * mm, "end": v(132.3, 15) * mm});
            skLineSegment(sketch, "E90.2.1", {"start": v(68.37, -15) * mm, "end": v(132.3, -15) * mm});
            skArc(sketch, "E90.2.2", {"start": v(132.3, -15) * mm, "mid": v(140.7, -30.9) * mm, "end": v(154.17, -42.8) * mm});
            skCircle(sketch, "E90.2.3", {"center": v(180, 0) * mm, "radius": 20 * mm});
            skArc(sketch, "E90.2.4", {"start": v(183.33, -49.89) * mm, "mid": v(210.9, -39.3) * mm, "end": v(227.7, -15) * mm});
            skArc(sketch, "E90.2.5", {"start": v(227.7, 15) * mm, "mid": v(210.9, 39.3) * mm, "end": v(183.33, 49.89) * mm});
            skArc(sketch, "E90.2.6", {"start": v(154.17, 42.8) * mm, "mid": v(140.7, 30.9) * mm, "end": v(132.3, 15) * mm});
            skLineSegment(sketch, "E90.2.7", {"start": v(227.7, 15) * mm, "end": v(279.6, 15) * mm});
            skLineSegment(sketch, "E90.2.8", {"start": v(227.7, -15) * mm, "end": v(279.6, -15) * mm});
            skLineSegment(sketch, "E90.3.0", {"start": v(37.74, 58.95) * mm, "end": v(82.95, 104.16) * mm});
            skLineSegment(sketch, "E90.3.1", {"start": v(58.95, 37.74) * mm, "end": v(104.16, 82.95) * mm});
            skArc(sketch, "E90.3.2", {"start": v(104.16, 82.95) * mm, "mid": v(121.34, 77.63) * mm, "end": v(139.28, 78.74) * mm});
            skCircle(sketch, "E90.3.3", {"center": v(127.28, 127.28) * mm, "radius": 20 * mm});
            skArc(sketch, "E90.3.4", {"start": v(164.91, 94.36) * mm, "mid": v(176.93, 121.34) * mm, "end": v(171.61, 150.4) * mm});
            skArc(sketch, "E90.3.5", {"start": v(150.4, 171.61) * mm, "mid": v(121.34, 176.93) * mm, "end": v(94.36, 164.91) * mm});
            skArc(sketch, "E90.3.6", {"start": v(78.74, 139.28) * mm, "mid": v(77.63, 121.34) * mm, "end": v(82.95, 104.16) * mm});
            skLineSegment(sketch, "E90.3.7", {"start": v(150.4, 171.61) * mm, "end": v(187.1, 208.31) * mm});
            skLineSegment(sketch, "E90.3.8", {"start": v(171.61, 150.4) * mm, "end": v(208.31, 187.1) * mm});
            skLineSegment(sketch, "E90.4.0", {"start": v(-15, 68.37) * mm, "end": v(-15, 132.3) * mm});
            skLineSegment(sketch, "E90.4.1", {"start": v(15, 68.37) * mm, "end": v(15, 132.3) * mm});
            skArc(sketch, "E90.4.2", {"start": v(15, 132.3) * mm, "mid": v(30.9, 140.7) * mm, "end": v(42.8, 154.17) * mm});
            skCircle(sketch, "E90.4.3", {"center": v(0, 180) * mm, "radius": 20 * mm});
            skArc(sketch, "E90.4.4", {"start": v(49.89, 183.33) * mm, "mid": v(39.3, 210.9) * mm, "end": v(15, 227.7) * mm});
            skArc(sketch, "E90.4.5", {"start": v(-15, 227.7) * mm, "mid": v(-39.3, 210.9) * mm, "end": v(-49.89, 183.33) * mm});
            skArc(sketch, "E90.4.6", {"start": v(-42.8, 154.17) * mm, "mid": v(-30.9, 140.7) * mm, "end": v(-15, 132.3) * mm});
            skLineSegment(sketch, "E90.4.7", {"start": v(-15, 227.7) * mm, "end": v(-15, 279.6) * mm});
            skLineSegment(sketch, "E90.4.8", {"start": v(15, 227.7) * mm, "end": v(15, 279.6) * mm});
            skLineSegment(sketch, "E90.5.0", {"start": v(-58.95, 37.74) * mm, "end": v(-104.16, 82.95) * mm});
            skLineSegment(sketch, "E90.5.1", {"start": v(-37.74, 58.95) * mm, "end": v(-82.95, 104.16) * mm});
            skArc(sketch, "E90.5.2", {"start": v(-82.95, 104.16) * mm, "mid": v(-77.63, 121.34) * mm, "end": v(-78.74, 139.28) * mm});
            skCircle(sketch, "E90.5.3", {"center": v(-127.28, 127.28) * mm, "radius": 20 * mm});
            skArc(sketch, "E90.5.4", {"start": v(-94.36, 164.91) * mm, "mid": v(-121.34, 176.93) * mm, "end": v(-150.4, 171.61) * mm});
            skArc(sketch, "E90.5.5", {"start": v(-171.61, 150.4) * mm, "mid": v(-176.93, 121.34) * mm, "end": v(-164.91, 94.36) * mm});
            skArc(sketch, "E90.5.6", {"start": v(-139.28, 78.74) * mm, "mid": v(-121.34, 77.63) * mm, "end": v(-104.16, 82.95) * mm});
            skLineSegment(sketch, "E90.5.7", {"start": v(-171.61, 150.4) * mm, "end": v(-208.31, 187.1) * mm});
            skLineSegment(sketch, "E90.5.8", {"start": v(-150.4, 171.61) * mm, "end": v(-187.1, 208.31) * mm});
            skLineSegment(sketch, "E90.6.0", {"start": v(-68.37, -15) * mm, "end": v(-132.3, -15) * mm});
            skLineSegment(sketch, "E90.6.1", {"start": v(-68.37, 15) * mm, "end": v(-132.3, 15) * mm});
            skArc(sketch, "E90.6.2", {"start": v(-132.3, 15) * mm, "mid": v(-140.7, 30.9) * mm, "end": v(-154.17, 42.8) * mm});
            skCircle(sketch, "E90.6.3", {"center": v(-180, 0) * mm, "radius": 20 * mm});
            skArc(sketch, "E90.6.4", {"start": v(-183.33, 49.89) * mm, "mid": v(-210.9, 39.3) * mm, "end": v(-227.7, 15) * mm});
            skArc(sketch, "E90.6.5", {"start": v(-227.7, -15) * mm, "mid": v(-210.9, -39.3) * mm, "end": v(-183.33, -49.89) * mm});
            skArc(sketch, "E90.6.6", {"start": v(-154.17, -42.8) * mm, "mid": v(-140.7, -30.9) * mm, "end": v(-132.3, -15) * mm});
            skLineSegment(sketch, "E90.6.7", {"start": v(-227.7, -15) * mm, "end": v(-279.6, -15) * mm});
            skLineSegment(sketch, "E90.6.8", {"start": v(-227.7, 15) * mm, "end": v(-279.6, 15) * mm});
            skLineSegment(sketch, "E90.7.0", {"start": v(-37.74, -58.95) * mm, "end": v(-82.95, -104.16) * mm});
            skLineSegment(sketch, "E90.7.1", {"start": v(-58.95, -37.74) * mm, "end": v(-104.16, -82.95) * mm});
            skArc(sketch, "E90.7.2", {"start": v(-104.16, -82.95) * mm, "mid": v(-121.34, -77.63) * mm, "end": v(-139.28, -78.74) * mm});
            skCircle(sketch, "E90.7.3", {"center": v(-127.28, -127.28) * mm, "radius": 20 * mm});
            skArc(sketch, "E90.7.4", {"start": v(-164.91, -94.36) * mm, "mid": v(-176.93, -121.34) * mm, "end": v(-171.61, -150.4) * mm});
            skArc(sketch, "E90.7.5", {"start": v(-150.4, -171.61) * mm, "mid": v(-121.34, -176.93) * mm, "end": v(-94.36, -164.91) * mm});
            skArc(sketch, "E90.7.6", {"start": v(-78.74, -139.28) * mm, "mid": v(-77.63, -121.34) * mm, "end": v(-82.95, -104.16) * mm});
            skLineSegment(sketch, "E90.7.7", {"start": v(-150.4, -171.61) * mm, "end": v(-187.1, -208.31) * mm});
            skLineSegment(sketch, "E90.7.8", {"start": v(-171.61, -150.4) * mm, "end": v(-208.31, -187.1) * mm});
            skArc(sketch, "E91.trimOffspring", {"start": v(-94.36, -164.91) * mm, "mid": v(-72.7, -175.54) * mm, "end": v(-49.89, -183.33) * mm});
            skArc(sketch, "E92.trimOffspring", {"start": v(-78.74, -139.28) * mm, "mid": v(-61.23, -147.82) * mm, "end": v(-42.8, -154.17) * mm});
            skArc(sketch, "E93.trimOffspring", {"start": v(-187.1, -208.31) * mm, "mid": v(-107.15, -258.69) * mm, "end": v(-15, -279.6) * mm});
            skArc(sketch, "E94.trimOffspring", {"start": v(-37.74, -58.95) * mm, "mid": v(-26.79, -64.67) * mm, "end": v(-15, -68.37) * mm});
            skArc(sketch, "E95.trimOffspring", {"start": v(-68.37, -15) * mm, "mid": v(-64.67, -26.79) * mm, "end": v(-58.95, -37.74) * mm});
            skArc(sketch, "E96.trimOffspring", {"start": v(-154.17, -42.8) * mm, "mid": v(-147.82, -61.23) * mm, "end": v(-139.28, -78.74) * mm});
            skArc(sketch, "E97.trimOffspring", {"start": v(-183.33, -49.89) * mm, "mid": v(-175.54, -72.7) * mm, "end": v(-164.91, -94.36) * mm});
            skArc(sketch, "E98.trimOffspring", {"start": v(-279.6, -15) * mm, "mid": v(-258.69, -107.15) * mm, "end": v(-208.31, -187.1) * mm});
            skArc(sketch, "E99.trimOffspring", {"start": v(-164.91, 94.36) * mm, "mid": v(-175.54, 72.7) * mm, "end": v(-183.33, 49.89) * mm});
            skArc(sketch, "E100.trimOffspring", {"start": v(-139.28, 78.74) * mm, "mid": v(-147.82, 61.23) * mm, "end": v(-154.17, 42.8) * mm});
            skArc(sketch, "E101.trimOffspring", {"start": v(-208.31, 187.1) * mm, "mid": v(-258.69, 107.15) * mm, "end": v(-279.6, 15) * mm});
            skArc(sketch, "E102.trimOffspring", {"start": v(-58.95, 37.74) * mm, "mid": v(-64.67, 26.79) * mm, "end": v(-68.37, 15) * mm});
            skArc(sketch, "E103.trimOffspring", {"start": v(-15, 68.37) * mm, "mid": v(-26.79, 64.67) * mm, "end": v(-37.74, 58.95) * mm});
            skArc(sketch, "E104.trimOffspring", {"start": v(-42.8, 154.17) * mm, "mid": v(-61.23, 147.82) * mm, "end": v(-78.74, 139.28) * mm});
            skArc(sketch, "E105.trimOffspring", {"start": v(-49.89, 183.33) * mm, "mid": v(-72.7, 175.54) * mm, "end": v(-94.36, 164.91) * mm});
            skArc(sketch, "E106.trimOffspring", {"start": v(78.74, 139.28) * mm, "mid": v(61.23, 147.82) * mm, "end": v(42.8, 154.17) * mm});
            skArc(sketch, "E107.trimOffspring", {"start": v(94.36, 164.91) * mm, "mid": v(72.7, 175.54) * mm, "end": v(49.89, 183.33) * mm});
            skArc(sketch, "E108.trimOffspring", {"start": v(183.33, 49.89) * mm, "mid": v(175.54, 72.7) * mm, "end": v(164.91, 94.36) * mm});
            skArc(sketch, "E109.trimOffspring", {"start": v(154.17, 42.8) * mm, "mid": v(147.82, 61.23) * mm, "end": v(139.28, 78.74) * mm});
            skArc(sketch, "E110.trimOffspring", {"start": v(68.37, 15) * mm, "mid": v(64.67, 26.79) * mm, "end": v(58.95, 37.74) * mm});
            skArc(sketch, "E111.trimOffspring", {"start": v(279.6, 15) * mm, "mid": v(258.69, 107.15) * mm, "end": v(208.31, 187.1) * mm});
            skArc(sketch, "E112.trimOffspring", {"start": v(58.95, -37.74) * mm, "mid": v(64.67, -26.79) * mm, "end": v(68.37, -15) * mm});
            skArc(sketch, "E113.trimOffspring", {"start": v(139.28, -78.74) * mm, "mid": v(147.82, -61.23) * mm, "end": v(154.17, -42.8) * mm});
            skArc(sketch, "E114.trimOffspring", {"start": v(164.91, -94.36) * mm, "mid": v(175.54, -72.7) * mm, "end": v(183.33, -49.89) * mm});
            skArc(sketch, "E115.trimOffspring", {"start": v(208.31, -187.1) * mm, "mid": v(258.69, -107.15) * mm, "end": v(279.6, -15) * mm});
            skArc(sketch, "E116.trimOffspring", {"start": v(37.74, 58.95) * mm, "mid": v(26.79, 64.67) * mm, "end": v(15, 68.37) * mm});
            skLineSegment(sketch, "E117.0", {"start": v(-4.9, 290) * mm, "end": v(-4.9, 300) * mm});
            skLineSegment(sketch, "E118.0", {"start": v(-1, 300) * mm, "end": v(-4.9, 300) * mm});
            skLineSegment(sketch, "E119.0", {"start": v(0, 301) * mm, "end": v(-1, 300) * mm});
            skLineSegment(sketch, "E120.0", {"start": v(0, 301) * mm, "end": v(1, 300) * mm});
            skLineSegment(sketch, "E121.0", {"start": v(4.9, 300) * mm, "end": v(1, 300) * mm});
            skLineSegment(sketch, "E122.0", {"start": v(4.9, 290) * mm, "end": v(4.9, 300) * mm});
            skLineSegment(sketch, "E123.0", {"start": v(-1, 290) * mm, "end": v(-4.9, 290) * mm});
            skLineSegment(sketch, "E124.0", {"start": v(0, 289) * mm, "end": v(-1, 290) * mm});
            skLineSegment(sketch, "E125.0", {"start": v(0, 289) * mm, "end": v(1, 290) * mm});
            skLineSegment(sketch, "E126.0", {"start": v(4.9, 290) * mm, "end": v(1, 290) * mm});
            skArc(sketch, "E127.trimOffspring", {"start": v(-15, 279.6) * mm, "mid": v(-107.15, 258.69) * mm, "end": v(-187.1, 208.31) * mm});
            skArc(sketch, "E128.trimOffspring", {"start": v(187.1, 208.31) * mm, "mid": v(107.15, 258.69) * mm, "end": v(15, 279.6) * mm});
            skLineSegment(sketch, "E129.1.0", {"start": v(-205.77, 204.35) * mm, "end": v(-208.53, 201.6) * mm});
            skLineSegment(sketch, "E129.1.1", {"start": v(-208.67, 215.6) * mm, "end": v(-211.42, 212.84) * mm});
            skLineSegment(sketch, "E129.1.2", {"start": v(-201.6, 208.53) * mm, "end": v(-204.35, 205.77) * mm});
            skLineSegment(sketch, "E129.1.3", {"start": v(-212.84, 211.42) * mm, "end": v(-215.6, 208.67) * mm});
            skLineSegment(sketch, "E129.1.4", {"start": v(-208.53, 201.6) * mm, "end": v(-215.6, 208.67) * mm});
            skLineSegment(sketch, "E129.1.5", {"start": v(-201.6, 208.53) * mm, "end": v(-208.67, 215.6) * mm});
            skLineSegment(sketch, "E129.1.6", {"start": v(-212.84, 212.84) * mm, "end": v(-211.42, 212.84) * mm});
            skLineSegment(sketch, "E129.1.7", {"start": v(-204.35, 204.35) * mm, "end": v(-204.35, 205.77) * mm});
            skLineSegment(sketch, "E129.1.8", {"start": v(-204.35, 204.35) * mm, "end": v(-205.77, 204.35) * mm});
            skLineSegment(sketch, "E129.1.9", {"start": v(-212.84, 212.84) * mm, "end": v(-212.84, 211.42) * mm});
            skLineSegment(sketch, "E129.2.0", {"start": v(-290, -1) * mm, "end": v(-290, -4.9) * mm});
            skLineSegment(sketch, "E129.2.1", {"start": v(-300, 4.9) * mm, "end": v(-300, 1) * mm});
            skLineSegment(sketch, "E129.2.2", {"start": v(-290, 4.9) * mm, "end": v(-290, 1) * mm});
            skLineSegment(sketch, "E129.2.3", {"start": v(-300, -1) * mm, "end": v(-300, -4.9) * mm});
            skLineSegment(sketch, "E129.2.4", {"start": v(-290, -4.9) * mm, "end": v(-300, -4.9) * mm});
            skLineSegment(sketch, "E129.2.5", {"start": v(-290, 4.9) * mm, "end": v(-300, 4.9) * mm});
            skLineSegment(sketch, "E129.2.6", {"start": v(-301, 0) * mm, "end": v(-300, 1) * mm});
            skLineSegment(sketch, "E129.2.7", {"start": v(-289, 0) * mm, "end": v(-290, 1) * mm});
            skLineSegment(sketch, "E129.2.8", {"start": v(-289, 0) * mm, "end": v(-290, -1) * mm});
            skLineSegment(sketch, "E129.2.9", {"start": v(-301, 0) * mm, "end": v(-300, -1) * mm});
            skLineSegment(sketch, "E129.3.0", {"start": v(-204.35, -205.77) * mm, "end": v(-201.6, -208.53) * mm});
            skLineSegment(sketch, "E129.3.1", {"start": v(-215.6, -208.67) * mm, "end": v(-212.84, -211.42) * mm});
            skLineSegment(sketch, "E129.3.2", {"start": v(-208.53, -201.6) * mm, "end": v(-205.77, -204.35) * mm});
            skLineSegment(sketch, "E129.3.3", {"start": v(-211.42, -212.84) * mm, "end": v(-208.67, -215.6) * mm});
            skLineSegment(sketch, "E129.3.4", {"start": v(-201.6, -208.53) * mm, "end": v(-208.67, -215.6) * mm});
            skLineSegment(sketch, "E129.3.5", {"start": v(-208.53, -201.6) * mm, "end": v(-215.6, -208.67) * mm});
            skLineSegment(sketch, "E129.3.6", {"start": v(-212.84, -212.84) * mm, "end": v(-212.84, -211.42) * mm});
            skLineSegment(sketch, "E129.3.7", {"start": v(-204.35, -204.35) * mm, "end": v(-205.77, -204.35) * mm});
            skLineSegment(sketch, "E129.3.8", {"start": v(-204.35, -204.35) * mm, "end": v(-204.35, -205.77) * mm});
            skLineSegment(sketch, "E129.3.9", {"start": v(-212.84, -212.84) * mm, "end": v(-211.42, -212.84) * mm});
            skLineSegment(sketch, "E129.4.0", {"start": v(1, -290) * mm, "end": v(4.9, -290) * mm});
            skLineSegment(sketch, "E129.4.1", {"start": v(-4.9, -300) * mm, "end": v(-1, -300) * mm});
            skLineSegment(sketch, "E129.4.2", {"start": v(-4.9, -290) * mm, "end": v(-1, -290) * mm});
            skLineSegment(sketch, "E129.4.3", {"start": v(1, -300) * mm, "end": v(4.9, -300) * mm});
            skLineSegment(sketch, "E129.4.4", {"start": v(4.9, -290) * mm, "end": v(4.9, -300) * mm});
            skLineSegment(sketch, "E129.4.5", {"start": v(-4.9, -290) * mm, "end": v(-4.9, -300) * mm});
            skLineSegment(sketch, "E129.4.6", {"start": v(0, -301) * mm, "end": v(-1, -300) * mm});
            skLineSegment(sketch, "E129.4.7", {"start": v(0, -289) * mm, "end": v(-1, -290) * mm});
            skLineSegment(sketch, "E129.4.8", {"start": v(0, -289) * mm, "end": v(1, -290) * mm});
            skLineSegment(sketch, "E129.4.9", {"start": v(0, -301) * mm, "end": v(1, -300) * mm});
            skLineSegment(sketch, "E129.5.0", {"start": v(205.77, -204.35) * mm, "end": v(208.53, -201.6) * mm});
            skLineSegment(sketch, "E129.5.1", {"start": v(208.67, -215.6) * mm, "end": v(211.42, -212.84) * mm});
            skLineSegment(sketch, "E129.5.2", {"start": v(201.6, -208.53) * mm, "end": v(204.35, -205.77) * mm});
            skLineSegment(sketch, "E129.5.3", {"start": v(212.84, -211.42) * mm, "end": v(215.6, -208.67) * mm});
            skLineSegment(sketch, "E129.5.4", {"start": v(208.53, -201.6) * mm, "end": v(215.6, -208.67) * mm});
            skLineSegment(sketch, "E129.5.5", {"start": v(201.6, -208.53) * mm, "end": v(208.67, -215.6) * mm});
            skLineSegment(sketch, "E129.5.6", {"start": v(212.84, -212.84) * mm, "end": v(211.42, -212.84) * mm});
            skLineSegment(sketch, "E129.5.7", {"start": v(204.35, -204.35) * mm, "end": v(204.35, -205.77) * mm});
            skLineSegment(sketch, "E129.5.8", {"start": v(204.35, -204.35) * mm, "end": v(205.77, -204.35) * mm});
            skLineSegment(sketch, "E129.5.9", {"start": v(212.84, -212.84) * mm, "end": v(212.84, -211.42) * mm});
            skLineSegment(sketch, "E129.6.0", {"start": v(290, 1) * mm, "end": v(290, 4.9) * mm});
            skLineSegment(sketch, "E129.6.1", {"start": v(300, -4.9) * mm, "end": v(300, -1) * mm});
            skLineSegment(sketch, "E129.6.2", {"start": v(290, -4.9) * mm, "end": v(290, -1) * mm});
            skLineSegment(sketch, "E129.6.3", {"start": v(300, 1) * mm, "end": v(300, 4.9) * mm});
            skLineSegment(sketch, "E129.6.4", {"start": v(290, 4.9) * mm, "end": v(300, 4.9) * mm});
            skLineSegment(sketch, "E129.6.5", {"start": v(290, -4.9) * mm, "end": v(300, -4.9) * mm});
            skLineSegment(sketch, "E129.6.6", {"start": v(301, 0) * mm, "end": v(300, -1) * mm});
            skLineSegment(sketch, "E129.6.7", {"start": v(289, 0) * mm, "end": v(290, -1) * mm});
            skLineSegment(sketch, "E129.6.8", {"start": v(289, 0) * mm, "end": v(290, 1) * mm});
            skLineSegment(sketch, "E129.6.9", {"start": v(301, 0) * mm, "end": v(300, 1) * mm});
            skLineSegment(sketch, "E129.7.0", {"start": v(204.35, 205.77) * mm, "end": v(201.6, 208.53) * mm});
            skLineSegment(sketch, "E129.7.1", {"start": v(215.6, 208.67) * mm, "end": v(212.84, 211.42) * mm});
            skLineSegment(sketch, "E129.7.2", {"start": v(208.53, 201.6) * mm, "end": v(205.77, 204.35) * mm});
            skLineSegment(sketch, "E129.7.3", {"start": v(211.42, 212.84) * mm, "end": v(208.67, 215.6) * mm});
            skLineSegment(sketch, "E129.7.4", {"start": v(201.6, 208.53) * mm, "end": v(208.67, 215.6) * mm});
            skLineSegment(sketch, "E129.7.5", {"start": v(208.53, 201.6) * mm, "end": v(215.6, 208.67) * mm});
            skLineSegment(sketch, "E129.7.6", {"start": v(212.84, 212.84) * mm, "end": v(212.84, 211.42) * mm});
            skLineSegment(sketch, "E129.7.7", {"start": v(204.35, 204.35) * mm, "end": v(205.77, 204.35) * mm});
            skLineSegment(sketch, "E129.7.8", {"start": v(204.35, 204.35) * mm, "end": v(204.35, 205.77) * mm});
            skLineSegment(sketch, "E129.7.9", {"start": v(212.84, 212.84) * mm, "end": v(211.42, 212.84) * mm});
            skSolve(sketch);
        }
        {
            var Q0;
            Q0=qSketchRegion(id+"F6",true);
            extrude(context, id + "F7", {"entities" : qUnion([Q0]), "depth" : 10 * mm, "offsetDistance" : 25 * mm});
        }
        {
            var Q0;
            Q0=qCreatedBy(id+"F1.planeOp",FACE);
            var sketch = newSketch(context, id + "F8", { "sketchPlane" : qUnion([Q0])});
            skCircle(sketch, "E130", {"center": v(0, 0) * mm, "radius": 575 * mm});
            skLineSegment(sketch, "E131.bottom", {"start": v(4.9, 530) * mm, "end": v(1, 530) * mm});
            skLineSegment(sketch, "E131.top", {"start": v(4.9, 540) * mm, "end": v(1, 540) * mm});
            skLineSegment(sketch, "E131.left", {"start": v(4.9, 530) * mm, "end": v(4.9, 540) * mm});
            skLineSegment(sketch, "E131.right", {"start": v(-4.9, 530) * mm, "end": v(-4.9, 540) * mm});
            skPoint(sketch, "E131.middle", {"position": v(0, 535) * mm});
            skLineSegment(sketch, "E132", {"start": v(0, 541) * mm, "end": v(-1, 540) * mm});
            skLineSegment(sketch, "E133", {"start": v(0, 541) * mm, "end": v(1, 540) * mm});
            skLineSegment(sketch, "E134.trimOffspring", {"start": v(-1, 540) * mm, "end": v(-4.9, 540) * mm});
            skLineSegment(sketch, "E135", {"start": v(0, 529) * mm, "end": v(-1, 530) * mm});
            skLineSegment(sketch, "E136", {"start": v(0, 529) * mm, "end": v(1, 530) * mm});
            skLineSegment(sketch, "E137.trimOffspring", {"start": v(-1, 530) * mm, "end": v(-4.9, 530) * mm});
            skPoint(sketch, "E138.2.0", {"position": v(-378.3, 378.3) * mm});
            skLineSegment(sketch, "E138.2.1", {"start": v(-378.23, 371.3) * mm, "end": v(-385.3, 378.37) * mm});
            skLineSegment(sketch, "E138.2.2", {"start": v(-371.3, 378.23) * mm, "end": v(-378.37, 385.3) * mm});
            skLineSegment(sketch, "E138.2.3", {"start": v(-371.3, 378.23) * mm, "end": v(-374.06, 375.47) * mm});
            skLineSegment(sketch, "E138.2.4", {"start": v(-374.06, 374.06) * mm, "end": v(-374.06, 375.47) * mm});
            skLineSegment(sketch, "E138.2.5", {"start": v(-374.06, 374.06) * mm, "end": v(-375.47, 374.06) * mm});
            skLineSegment(sketch, "E138.2.6", {"start": v(-375.47, 374.06) * mm, "end": v(-378.23, 371.3) * mm});
            skLineSegment(sketch, "E138.2.7", {"start": v(-378.37, 385.3) * mm, "end": v(-381.13, 382.54) * mm});
            skLineSegment(sketch, "E138.2.8", {"start": v(-382.54, 381.13) * mm, "end": v(-385.3, 378.37) * mm});
            skLineSegment(sketch, "E138.2.9", {"start": v(-382.54, 382.54) * mm, "end": v(-381.13, 382.54) * mm});
            skLineSegment(sketch, "E138.2.10", {"start": v(-382.54, 382.54) * mm, "end": v(-382.54, 381.13) * mm});
            skPoint(sketch, "E138.4.0", {"position": v(-535, 0) * mm});
            skLineSegment(sketch, "E138.4.1", {"start": v(-530, -4.9) * mm, "end": v(-540, -4.9) * mm});
            skLineSegment(sketch, "E138.4.2", {"start": v(-530, 4.9) * mm, "end": v(-540, 4.9) * mm});
            skLineSegment(sketch, "E138.4.3", {"start": v(-530, 4.9) * mm, "end": v(-530, 1) * mm});
            skLineSegment(sketch, "E138.4.4", {"start": v(-529, 0) * mm, "end": v(-530, 1) * mm});
            skLineSegment(sketch, "E138.4.5", {"start": v(-529, 0) * mm, "end": v(-530, -1) * mm});
            skLineSegment(sketch, "E138.4.6", {"start": v(-530, -1) * mm, "end": v(-530, -4.9) * mm});
            skLineSegment(sketch, "E138.4.7", {"start": v(-540, 4.9) * mm, "end": v(-540, 1) * mm});
            skLineSegment(sketch, "E138.4.8", {"start": v(-540, -1) * mm, "end": v(-540, -4.9) * mm});
            skLineSegment(sketch, "E138.4.9", {"start": v(-541, 0) * mm, "end": v(-540, 1) * mm});
            skLineSegment(sketch, "E138.4.10", {"start": v(-541, 0) * mm, "end": v(-540, -1) * mm});
            skPoint(sketch, "E138.6.0", {"position": v(-378.3, -378.3) * mm});
            skLineSegment(sketch, "E138.6.1", {"start": v(-371.3, -378.23) * mm, "end": v(-378.37, -385.3) * mm});
            skLineSegment(sketch, "E138.6.2", {"start": v(-378.23, -371.3) * mm, "end": v(-385.3, -378.37) * mm});
            skLineSegment(sketch, "E138.6.3", {"start": v(-378.23, -371.3) * mm, "end": v(-375.47, -374.06) * mm});
            skLineSegment(sketch, "E138.6.4", {"start": v(-374.06, -374.06) * mm, "end": v(-375.47, -374.06) * mm});
            skLineSegment(sketch, "E138.6.5", {"start": v(-374.06, -374.06) * mm, "end": v(-374.06, -375.47) * mm});
            skLineSegment(sketch, "E138.6.6", {"start": v(-374.06, -375.47) * mm, "end": v(-371.3, -378.23) * mm});
            skLineSegment(sketch, "E138.6.7", {"start": v(-385.3, -378.37) * mm, "end": v(-382.54, -381.13) * mm});
            skLineSegment(sketch, "E138.6.8", {"start": v(-381.13, -382.54) * mm, "end": v(-378.37, -385.3) * mm});
            skLineSegment(sketch, "E138.6.9", {"start": v(-382.54, -382.54) * mm, "end": v(-382.54, -381.13) * mm});
            skLineSegment(sketch, "E138.6.10", {"start": v(-382.54, -382.54) * mm, "end": v(-381.13, -382.54) * mm});
            skPoint(sketch, "E138.8.0", {"position": v(0, -535) * mm});
            skLineSegment(sketch, "E138.8.1", {"start": v(4.9, -530) * mm, "end": v(4.9, -540) * mm});
            skLineSegment(sketch, "E138.8.2", {"start": v(-4.9, -530) * mm, "end": v(-4.9, -540) * mm});
            skLineSegment(sketch, "E138.8.3", {"start": v(-4.9, -530) * mm, "end": v(-1, -530) * mm});
            skLineSegment(sketch, "E138.8.4", {"start": v(0, -529) * mm, "end": v(-1, -530) * mm});
            skLineSegment(sketch, "E138.8.5", {"start": v(0, -529) * mm, "end": v(1, -530) * mm});
            skLineSegment(sketch, "E138.8.6", {"start": v(1, -530) * mm, "end": v(4.9, -530) * mm});
            skLineSegment(sketch, "E138.8.7", {"start": v(-4.9, -540) * mm, "end": v(-1, -540) * mm});
            skLineSegment(sketch, "E138.8.8", {"start": v(1, -540) * mm, "end": v(4.9, -540) * mm});
            skLineSegment(sketch, "E138.8.9", {"start": v(0, -541) * mm, "end": v(-1, -540) * mm});
            skLineSegment(sketch, "E138.8.10", {"start": v(0, -541) * mm, "end": v(1, -540) * mm});
            skPoint(sketch, "E138.10.0", {"position": v(378.3, -378.3) * mm});
            skLineSegment(sketch, "E138.10.1", {"start": v(378.23, -371.3) * mm, "end": v(385.3, -378.37) * mm});
            skLineSegment(sketch, "E138.10.2", {"start": v(371.3, -378.23) * mm, "end": v(378.37, -385.3) * mm});
            skLineSegment(sketch, "E138.10.3", {"start": v(371.3, -378.23) * mm, "end": v(374.06, -375.47) * mm});
            skLineSegment(sketch, "E138.10.4", {"start": v(374.06, -374.06) * mm, "end": v(374.06, -375.47) * mm});
            skLineSegment(sketch, "E138.10.5", {"start": v(374.06, -374.06) * mm, "end": v(375.47, -374.06) * mm});
            skLineSegment(sketch, "E138.10.6", {"start": v(375.47, -374.06) * mm, "end": v(378.23, -371.3) * mm});
            skLineSegment(sketch, "E138.10.7", {"start": v(378.37, -385.3) * mm, "end": v(381.13, -382.54) * mm});
            skLineSegment(sketch, "E138.10.8", {"start": v(382.54, -381.13) * mm, "end": v(385.3, -378.37) * mm});
            skLineSegment(sketch, "E138.10.9", {"start": v(382.54, -382.54) * mm, "end": v(381.13, -382.54) * mm});
            skLineSegment(sketch, "E138.10.10", {"start": v(382.54, -382.54) * mm, "end": v(382.54, -381.13) * mm});
            skPoint(sketch, "E138.12.0", {"position": v(535, 0) * mm});
            skLineSegment(sketch, "E138.12.1", {"start": v(530, 4.9) * mm, "end": v(540, 4.9) * mm});
            skLineSegment(sketch, "E138.12.2", {"start": v(530, -4.9) * mm, "end": v(540, -4.9) * mm});
            skLineSegment(sketch, "E138.12.3", {"start": v(530, -4.9) * mm, "end": v(530, -1) * mm});
            skLineSegment(sketch, "E138.12.4", {"start": v(529, 0) * mm, "end": v(530, -1) * mm});
            skLineSegment(sketch, "E138.12.5", {"start": v(529, 0) * mm, "end": v(530, 1) * mm});
            skLineSegment(sketch, "E138.12.6", {"start": v(530, 1) * mm, "end": v(530, 4.9) * mm});
            skLineSegment(sketch, "E138.12.7", {"start": v(540, -4.9) * mm, "end": v(540, -1) * mm});
            skLineSegment(sketch, "E138.12.8", {"start": v(540, 1) * mm, "end": v(540, 4.9) * mm});
            skLineSegment(sketch, "E138.12.9", {"start": v(541, 0) * mm, "end": v(540, -1) * mm});
            skLineSegment(sketch, "E138.12.10", {"start": v(541, 0) * mm, "end": v(540, 1) * mm});
            skPoint(sketch, "E138.14.0", {"position": v(378.3, 378.3) * mm});
            skLineSegment(sketch, "E138.14.1", {"start": v(371.3, 378.23) * mm, "end": v(378.37, 385.3) * mm});
            skLineSegment(sketch, "E138.14.2", {"start": v(378.23, 371.3) * mm, "end": v(385.3, 378.37) * mm});
            skLineSegment(sketch, "E138.14.3", {"start": v(378.23, 371.3) * mm, "end": v(375.47, 374.06) * mm});
            skLineSegment(sketch, "E138.14.4", {"start": v(374.06, 374.06) * mm, "end": v(375.47, 374.06) * mm});
            skLineSegment(sketch, "E138.14.5", {"start": v(374.06, 374.06) * mm, "end": v(374.06, 375.47) * mm});
            skLineSegment(sketch, "E138.14.6", {"start": v(374.06, 375.47) * mm, "end": v(371.3, 378.23) * mm});
            skLineSegment(sketch, "E138.14.7", {"start": v(385.3, 378.37) * mm, "end": v(382.54, 381.13) * mm});
            skLineSegment(sketch, "E138.14.8", {"start": v(381.13, 382.54) * mm, "end": v(378.37, 385.3) * mm});
            skLineSegment(sketch, "E138.14.9", {"start": v(382.54, 382.54) * mm, "end": v(382.54, 381.13) * mm});
            skLineSegment(sketch, "E138.14.10", {"start": v(382.54, 382.54) * mm, "end": v(381.13, 382.54) * mm});
            skCircle(sketch, "E139", {"center": v(0, 0) * mm, "radius": 475 * mm});
            skLineSegment(sketch, "E140.bottom", {"start": v(4.9, 500) * mm, "end": v(1, 500) * mm});
            skLineSegment(sketch, "E140.top", {"start": v(4.9, 510) * mm, "end": v(1, 510) * mm});
            skLineSegment(sketch, "E140.left", {"start": v(4.9, 500) * mm, "end": v(4.9, 510) * mm});
            skLineSegment(sketch, "E140.right", {"start": v(-4.9, 500) * mm, "end": v(-4.9, 510) * mm});
            skPoint(sketch, "E140.middle", {"position": v(0, 505) * mm});
            skLineSegment(sketch, "E141", {"start": v(0, 511) * mm, "end": v(-1, 510) * mm});
            skLineSegment(sketch, "E142", {"start": v(0, 511) * mm, "end": v(1, 510) * mm});
            skLineSegment(sketch, "E143.trimOffspring", {"start": v(-1, 510) * mm, "end": v(-4.9, 510) * mm});
            skLineSegment(sketch, "E144", {"start": v(0, 499) * mm, "end": v(-1, 500) * mm});
            skLineSegment(sketch, "E145", {"start": v(0, 499) * mm, "end": v(1, 500) * mm});
            skLineSegment(sketch, "E146.trimOffspring", {"start": v(-1, 500) * mm, "end": v(-4.9, 500) * mm});
            skLineSegment(sketch, "E147.1.0", {"start": v(-350.09, 357.02) * mm, "end": v(-357.16, 364.09) * mm});
            skPoint(sketch, "E147.1.1", {"position": v(-357.09, 357.09) * mm});
            skLineSegment(sketch, "E147.1.2", {"start": v(-357.02, 350.09) * mm, "end": v(-364.09, 357.16) * mm});
            skLineSegment(sketch, "E147.1.3", {"start": v(-357.16, 364.09) * mm, "end": v(-359.92, 361.33) * mm});
            skLineSegment(sketch, "E147.1.4", {"start": v(-350.09, 357.02) * mm, "end": v(-352.85, 354.26) * mm});
            skLineSegment(sketch, "E147.1.5", {"start": v(-361.33, 361.33) * mm, "end": v(-361.33, 359.92) * mm});
            skLineSegment(sketch, "E147.1.6", {"start": v(-361.33, 361.33) * mm, "end": v(-359.92, 361.33) * mm});
            skLineSegment(sketch, "E147.1.7", {"start": v(-354.26, 352.85) * mm, "end": v(-357.02, 350.09) * mm});
            skLineSegment(sketch, "E147.1.8", {"start": v(-361.33, 359.92) * mm, "end": v(-364.09, 357.16) * mm});
            skLineSegment(sketch, "E147.1.9", {"start": v(-352.85, 352.85) * mm, "end": v(-352.85, 354.26) * mm});
            skLineSegment(sketch, "E147.1.10", {"start": v(-352.85, 352.85) * mm, "end": v(-354.26, 352.85) * mm});
            skLineSegment(sketch, "E147.2.0", {"start": v(-500, 4.9) * mm, "end": v(-510, 4.9) * mm});
            skPoint(sketch, "E147.2.1", {"position": v(-505, 0) * mm});
            skLineSegment(sketch, "E147.2.2", {"start": v(-500, -4.9) * mm, "end": v(-510, -4.9) * mm});
            skLineSegment(sketch, "E147.2.3", {"start": v(-510, 4.9) * mm, "end": v(-510, 1) * mm});
            skLineSegment(sketch, "E147.2.4", {"start": v(-500, 4.9) * mm, "end": v(-500, 1) * mm});
            skLineSegment(sketch, "E147.2.5", {"start": v(-511, 0) * mm, "end": v(-510, -1) * mm});
            skLineSegment(sketch, "E147.2.6", {"start": v(-511, 0) * mm, "end": v(-510, 1) * mm});
            skLineSegment(sketch, "E147.2.7", {"start": v(-500, -1) * mm, "end": v(-500, -4.9) * mm});
            skLineSegment(sketch, "E147.2.8", {"start": v(-510, -1) * mm, "end": v(-510, -4.9) * mm});
            skLineSegment(sketch, "E147.2.9", {"start": v(-499, 0) * mm, "end": v(-500, 1) * mm});
            skLineSegment(sketch, "E147.2.10", {"start": v(-499, 0) * mm, "end": v(-500, -1) * mm});
            skLineSegment(sketch, "E147.3.0", {"start": v(-357.02, -350.09) * mm, "end": v(-364.09, -357.16) * mm});
            skPoint(sketch, "E147.3.1", {"position": v(-357.09, -357.09) * mm});
            skLineSegment(sketch, "E147.3.2", {"start": v(-350.09, -357.02) * mm, "end": v(-357.16, -364.09) * mm});
            skLineSegment(sketch, "E147.3.3", {"start": v(-364.09, -357.16) * mm, "end": v(-361.33, -359.92) * mm});
            skLineSegment(sketch, "E147.3.4", {"start": v(-357.02, -350.09) * mm, "end": v(-354.26, -352.85) * mm});
            skLineSegment(sketch, "E147.3.5", {"start": v(-361.33, -361.33) * mm, "end": v(-359.92, -361.33) * mm});
            skLineSegment(sketch, "E147.3.6", {"start": v(-361.33, -361.33) * mm, "end": v(-361.33, -359.92) * mm});
            skLineSegment(sketch, "E147.3.7", {"start": v(-352.85, -354.26) * mm, "end": v(-350.09, -357.02) * mm});
            skLineSegment(sketch, "E147.3.8", {"start": v(-359.92, -361.33) * mm, "end": v(-357.16, -364.09) * mm});
            skLineSegment(sketch, "E147.3.9", {"start": v(-352.85, -352.85) * mm, "end": v(-354.26, -352.85) * mm});
            skLineSegment(sketch, "E147.3.10", {"start": v(-352.85, -352.85) * mm, "end": v(-352.85, -354.26) * mm});
            skLineSegment(sketch, "E147.4.0", {"start": v(-4.9, -500) * mm, "end": v(-4.9, -510) * mm});
            skPoint(sketch, "E147.4.1", {"position": v(0, -505) * mm});
            skLineSegment(sketch, "E147.4.2", {"start": v(4.9, -500) * mm, "end": v(4.9, -510) * mm});
            skLineSegment(sketch, "E147.4.3", {"start": v(-4.9, -510) * mm, "end": v(-1, -510) * mm});
            skLineSegment(sketch, "E147.4.4", {"start": v(-4.9, -500) * mm, "end": v(-1, -500) * mm});
            skLineSegment(sketch, "E147.4.5", {"start": v(0, -511) * mm, "end": v(1, -510) * mm});
            skLineSegment(sketch, "E147.4.6", {"start": v(0, -511) * mm, "end": v(-1, -510) * mm});
            skLineSegment(sketch, "E147.4.7", {"start": v(1, -500) * mm, "end": v(4.9, -500) * mm});
            skLineSegment(sketch, "E147.4.8", {"start": v(1, -510) * mm, "end": v(4.9, -510) * mm});
            skLineSegment(sketch, "E147.4.9", {"start": v(0, -499) * mm, "end": v(-1, -500) * mm});
            skLineSegment(sketch, "E147.4.10", {"start": v(0, -499) * mm, "end": v(1, -500) * mm});
            skLineSegment(sketch, "E147.5.0", {"start": v(350.09, -357.02) * mm, "end": v(357.16, -364.09) * mm});
            skPoint(sketch, "E147.5.1", {"position": v(357.09, -357.09) * mm});
            skLineSegment(sketch, "E147.5.2", {"start": v(357.02, -350.09) * mm, "end": v(364.09, -357.16) * mm});
            skLineSegment(sketch, "E147.5.3", {"start": v(357.16, -364.09) * mm, "end": v(359.92, -361.33) * mm});
            skLineSegment(sketch, "E147.5.4", {"start": v(350.09, -357.02) * mm, "end": v(352.85, -354.26) * mm});
            skLineSegment(sketch, "E147.5.5", {"start": v(361.33, -361.33) * mm, "end": v(361.33, -359.92) * mm});
            skLineSegment(sketch, "E147.5.6", {"start": v(361.33, -361.33) * mm, "end": v(359.92, -361.33) * mm});
            skLineSegment(sketch, "E147.5.7", {"start": v(354.26, -352.85) * mm, "end": v(357.02, -350.09) * mm});
            skLineSegment(sketch, "E147.5.8", {"start": v(361.33, -359.92) * mm, "end": v(364.09, -357.16) * mm});
            skLineSegment(sketch, "E147.5.9", {"start": v(352.85, -352.85) * mm, "end": v(352.85, -354.26) * mm});
            skLineSegment(sketch, "E147.5.10", {"start": v(352.85, -352.85) * mm, "end": v(354.26, -352.85) * mm});
            skLineSegment(sketch, "E147.6.0", {"start": v(500, -4.9) * mm, "end": v(510, -4.9) * mm});
            skPoint(sketch, "E147.6.1", {"position": v(505, 0) * mm});
            skLineSegment(sketch, "E147.6.2", {"start": v(500, 4.9) * mm, "end": v(510, 4.9) * mm});
            skLineSegment(sketch, "E147.6.3", {"start": v(510, -4.9) * mm, "end": v(510, -1) * mm});
            skLineSegment(sketch, "E147.6.4", {"start": v(500, -4.9) * mm, "end": v(500, -1) * mm});
            skLineSegment(sketch, "E147.6.5", {"start": v(511, 0) * mm, "end": v(510, 1) * mm});
            skLineSegment(sketch, "E147.6.6", {"start": v(511, 0) * mm, "end": v(510, -1) * mm});
            skLineSegment(sketch, "E147.6.7", {"start": v(500, 1) * mm, "end": v(500, 4.9) * mm});
            skLineSegment(sketch, "E147.6.8", {"start": v(510, 1) * mm, "end": v(510, 4.9) * mm});
            skLineSegment(sketch, "E147.6.9", {"start": v(499, 0) * mm, "end": v(500, -1) * mm});
            skLineSegment(sketch, "E147.6.10", {"start": v(499, 0) * mm, "end": v(500, 1) * mm});
            skLineSegment(sketch, "E147.7.0", {"start": v(357.02, 350.09) * mm, "end": v(364.09, 357.16) * mm});
            skPoint(sketch, "E147.7.1", {"position": v(357.09, 357.09) * mm});
            skLineSegment(sketch, "E147.7.2", {"start": v(350.09, 357.02) * mm, "end": v(357.16, 364.09) * mm});
            skLineSegment(sketch, "E147.7.3", {"start": v(364.09, 357.16) * mm, "end": v(361.33, 359.92) * mm});
            skLineSegment(sketch, "E147.7.4", {"start": v(357.02, 350.09) * mm, "end": v(354.26, 352.85) * mm});
            skLineSegment(sketch, "E147.7.5", {"start": v(361.33, 361.33) * mm, "end": v(359.92, 361.33) * mm});
            skLineSegment(sketch, "E147.7.6", {"start": v(361.33, 361.33) * mm, "end": v(361.33, 359.92) * mm});
            skLineSegment(sketch, "E147.7.7", {"start": v(352.85, 354.26) * mm, "end": v(350.09, 357.02) * mm});
            skLineSegment(sketch, "E147.7.8", {"start": v(359.92, 361.33) * mm, "end": v(357.16, 364.09) * mm});
            skLineSegment(sketch, "E147.7.9", {"start": v(352.85, 352.85) * mm, "end": v(354.26, 352.85) * mm});
            skLineSegment(sketch, "E147.7.10", {"start": v(352.85, 352.85) * mm, "end": v(352.85, 354.26) * mm});
            skSolve(sketch);
        }
        {
            var Q0;
            Q0=qSketchRegion(id+"F8",true);
            extrude(context, id + "F9", {"entities" : qUnion([Q0]), "depth" : 10 * mm, "offsetDistance" : 25 * mm});
        }
        {
            var Q0;
            Q0=qCreatedBy(makeId("Right.planeOp"),FACE);
            var sketch = newSketch(context, id + "F10", { "sketchPlane" : qUnion([Q0])});
            skLineSegment(sketch, "E148.0.1", {"start": v(540, 0) * mm, "end": v(540, 10) * mm});
            skLineSegment(sketch, "E148.0.2", {"start": v(540, 10) * mm, "end": v(530, 10) * mm});
            skLineSegment(sketch, "E148.0.3", {"start": v(530, 10) * mm, "end": v(530, 0) * mm});
            skLineSegment(sketch, "E149.0.0", {"start": v(530, -200) * mm, "end": v(540, -200) * mm});
            skLineSegment(sketch, "E149.0.1", {"start": v(540, -200) * mm, "end": v(540, -190) * mm});
            skLineSegment(sketch, "E149.0.3", {"start": v(530, -190) * mm, "end": v(530, -200) * mm});
            skLineSegment(sketch, "E150", {"start": v(530, 0) * mm, "end": v(520, 0) * mm});
            skLineSegment(sketch, "E151", {"start": v(520, 0) * mm, "end": v(520, -90.1) * mm});
            skLineSegment(sketch, "E152", {"start": v(520, -190) * mm, "end": v(530, -190) * mm});
            skLineSegment(sketch, "E153", {"start": v(540, -190) * mm, "end": v(550, -190) * mm});
            skLineSegment(sketch, "E154", {"start": v(550, -190) * mm, "end": v(550, 0) * mm});
            skLineSegment(sketch, "E155", {"start": v(550, 0) * mm, "end": v(540, 0) * mm});
            skLineSegment(sketch, "E156.0.0", {"start": v(290, 0) * mm, "end": v(300, 0) * mm});
            skLineSegment(sketch, "E156.0.1", {"start": v(300, 0) * mm, "end": v(300, 10) * mm});
            skLineSegment(sketch, "E156.0.3", {"start": v(290, 10) * mm, "end": v(290, 0) * mm});
            skLineSegment(sketch, "E157.0.1", {"start": v(300, 200) * mm, "end": v(300, 210) * mm});
            skLineSegment(sketch, "E157.0.2", {"start": v(300, 210) * mm, "end": v(290, 210) * mm});
            skLineSegment(sketch, "E157.0.3", {"start": v(290, 210) * mm, "end": v(290, 200) * mm});
            skLineSegment(sketch, "E158", {"start": v(290, 200) * mm, "end": v(280, 200) * mm});
            skLineSegment(sketch, "E159", {"start": v(280, 200) * mm, "end": v(280, 109.9) * mm});
            skLineSegment(sketch, "E160", {"start": v(280, 10) * mm, "end": v(290, 10) * mm});
            skLineSegment(sketch, "E161", {"start": v(300, 10) * mm, "end": v(310, 10) * mm});
            skLineSegment(sketch, "E162", {"start": v(310, 10) * mm, "end": v(310, 200) * mm});
            skLineSegment(sketch, "E163", {"start": v(310, 200) * mm, "end": v(300, 200) * mm});
            skLineSegment(sketch, "E164", {"start": v(280, 109.9) * mm, "end": v(290, 109.9) * mm});
            skLineSegment(sketch, "E165", {"start": v(290, 109.9) * mm, "end": v(290, 100.1) * mm});
            skLineSegment(sketch, "E166", {"start": v(290, 100.1) * mm, "end": v(280, 100.1) * mm});
            skLineSegment(sketch, "E167.trimOffspring", {"start": v(280, 100.1) * mm, "end": v(280, 10) * mm});
            skLineSegment(sketch, "E168", {"start": v(520, -90.1) * mm, "end": v(530, -90.1) * mm});
            skLineSegment(sketch, "E169", {"start": v(530, -90.1) * mm, "end": v(530, -99.9) * mm});
            skLineSegment(sketch, "E170", {"start": v(530, -99.9) * mm, "end": v(520, -99.9) * mm});
            skLineSegment(sketch, "E171.trimOffspring", {"start": v(520, -99.9) * mm, "end": v(520, -190) * mm});
            skLineSegment(sketch, "E172.0", {"start": v(-475, -190) * mm, "end": v(475, -190) * mm, "construction": true});
            skLineSegment(sketch, "E173", {"start": v(513.03, -190) * mm, "end": v(510, -190) * mm});
            skLineSegment(sketch, "E174", {"start": v(510, -190) * mm, "end": v(510, -200) * mm});
            skLineSegment(sketch, "E175", {"start": v(510, -200) * mm, "end": v(500, -200) * mm});
            skLineSegment(sketch, "E176", {"start": v(500, -200) * mm, "end": v(500, -190) * mm});
            skLineSegment(sketch, "E177", {"start": v(500, -190) * mm, "end": v(490, -190) * mm});
            skLineSegment(sketch, "E178", {"start": v(320, 10) * mm, "end": v(320, 0) * mm});
            skLineSegment(sketch, "E179", {"start": v(330, 0) * mm, "end": v(330, 10) * mm});
            skLineSegment(sketch, "E180", {"start": v(330, 10) * mm, "end": v(320, 10) * mm});
            skLineSegment(sketch, "E181", {"start": v(320, 0) * mm, "end": v(310, 0) * mm});
            skLineSegment(sketch, "E182", {"start": v(330, 0) * mm, "end": v(340, 0) * mm});
            skLineSegment(sketch, "E183", {"start": v(340, 0) * mm, "end": v(515.2, -184.94) * mm});
            skLineSegment(sketch, "E184", {"start": v(490, -190) * mm, "end": v(310, 0) * mm});
            skPoint(sketch, "E185.visualSharp", {"position": v(520, -190) * mm});
            skArc(sketch, "E185.filletArc", {"start": v(513.03, -190) * mm, "mid": v(515.78, -188.19) * mm, "end": v(515.2, -184.94) * mm});
            skSolve(sketch);
        }
        {
            var Q0;
            Q0=qSketchRegion(id+"F10",true);
            extrude(context, id + "F11", {"entities" : qUnion([Q0]), "endBound" : BoundingType.SYMMETRIC, "depth" : 10 * mm, "offsetDistance" : 25 * mm});
        }
        {
            var Q0;
            Q0=makeQuery(id+"F11.opExtrude","SWEPT_BODY",BODY,{"disambiguationData":[OSD([sQuery(id+"F10.wireOp",EDGE,"E148.0.1"),sQuery(id+"F10.wireOp",EDGE,"E148.0.2"),sQuery(id+"F10.wireOp",EDGE,"E148.0.3"),sQuery(id+"F10.wireOp",EDGE,"E149.0.0"),sQuery(id+"F10.wireOp",EDGE,"E149.0.1"),sQuery(id+"F10.wireOp",EDGE,"E149.0.3"),sQuery(id+"F10.wireOp",EDGE,"E150"),sQuery(id+"F10.wireOp",EDGE,"E151"),sQuery(id+"F10.wireOp",EDGE,"E152"),sQuery(id+"F10.wireOp",EDGE,"E153"),sQuery(id+"F10.wireOp",EDGE,"E154"),sQuery(id+"F10.wireOp",EDGE,"E155")])]});
            var Q1;
            Q1=makeQuery(id+"F11.opExtrude","SWEPT_BODY",BODY,{"disambiguationData":[OSD([sQuery(id+"F10.wireOp",EDGE,"E156.0.0"),sQuery(id+"F10.wireOp",EDGE,"E156.0.1"),sQuery(id+"F10.wireOp",EDGE,"E156.0.3"),sQuery(id+"F10.wireOp",EDGE,"E157.0.1"),sQuery(id+"F10.wireOp",EDGE,"E157.0.2"),sQuery(id+"F10.wireOp",EDGE,"E157.0.3"),sQuery(id+"F10.wireOp",EDGE,"E158"),sQuery(id+"F10.wireOp",EDGE,"E159"),sQuery(id+"F10.wireOp",EDGE,"E160"),sQuery(id+"F10.wireOp",EDGE,"E161"),sQuery(id+"F10.wireOp",EDGE,"E162"),sQuery(id+"F10.wireOp",EDGE,"E163")])]});
            var Q2;
            Q2=makeQuery(id+"F7.opExtrude","CAP_EDGE",EDGE,{"disambiguationData":[OSD([sQuery(id+"F6.wireOp",EDGE,"E78.0")])],"isStart":false});
            circularPattern(context, id + "F12", {"operationType" : NewBodyOperationType.ADD, "entities" : qUnion([Q0, Q1]), "axis" : qUnion([Q2]), "angle" : 360 * degree, "instanceCount" : 8, "equalSpace" : true});
        }
        {
            var Q0;
            Q0=qCreatedBy(id+"F2.planeOp",FACE);
            var sketch = newSketch(context, id + "F13", { "sketchPlane" : qUnion([Q0])});
            skPoint(sketch, "E186.0", {"position": v(-520, 0) * mm});
            skPoint(sketch, "E187.0", {"position": v(-540, 0) * mm});
            skPoint(sketch, "E188.0", {"position": v(-530, -5) * mm});
            skPoint(sketch, "E189.0", {"position": v(-530, 5) * mm});
            skArc(sketch, "E190", {"start": v(-539.98, -5) * mm, "mid": v(-498.9, -206.65) * mm, "end": v(-385.36, -378.29) * mm});
            skCircle(sketch, "E191", {"center": v(0, 0) * mm, "radius": 520 * mm});
            skLineSegment(sketch, "E192", {"start": v(-530, 5) * mm, "end": v(-530, -5) * mm});
            skLineSegment(sketch, "E193", {"start": v(-530, 5) * mm, "end": v(-539.98, 5) * mm});
            skLineSegment(sketch, "E194", {"start": v(-530, -5) * mm, "end": v(-539.98, -5) * mm});
            skLineSegment(sketch, "E195", {"start": v(-540, 0) * mm, "end": v(-520, 0) * mm, "construction": true});
            skLineSegment(sketch, "E196.1.0", {"start": v(-378.3, -371.23) * mm, "end": v(-385.36, -378.29) * mm});
            skLineSegment(sketch, "E196.1.1", {"start": v(-378.3, -371.23) * mm, "end": v(-371.23, -378.3) * mm});
            skLineSegment(sketch, "E196.1.2", {"start": v(-381.84, -381.84) * mm, "end": v(-367.7, -367.7) * mm, "construction": true});
            skLineSegment(sketch, "E196.1.3", {"start": v(-371.23, -378.3) * mm, "end": v(-378.29, -385.36) * mm});
            skLineSegment(sketch, "E196.2.0", {"start": v(-5, -530) * mm, "end": v(-5, -539.98) * mm});
            skLineSegment(sketch, "E196.2.1", {"start": v(-5, -530) * mm, "end": v(5, -530) * mm});
            skLineSegment(sketch, "E196.2.2", {"start": v(0, -540) * mm, "end": v(0, -520) * mm, "construction": true});
            skLineSegment(sketch, "E196.2.3", {"start": v(5, -530) * mm, "end": v(5, -539.98) * mm});
            skLineSegment(sketch, "E196.3.0", {"start": v(371.23, -378.3) * mm, "end": v(378.29, -385.36) * mm});
            skLineSegment(sketch, "E196.3.1", {"start": v(371.23, -378.3) * mm, "end": v(378.3, -371.23) * mm});
            skLineSegment(sketch, "E196.3.2", {"start": v(381.84, -381.84) * mm, "end": v(367.7, -367.7) * mm, "construction": true});
            skLineSegment(sketch, "E196.3.3", {"start": v(378.3, -371.23) * mm, "end": v(385.36, -378.29) * mm});
            skLineSegment(sketch, "E196.4.0", {"start": v(530, -5) * mm, "end": v(539.98, -5) * mm});
            skLineSegment(sketch, "E196.4.1", {"start": v(530, -5) * mm, "end": v(530, 5) * mm});
            skLineSegment(sketch, "E196.4.2", {"start": v(540, 0) * mm, "end": v(520, 0) * mm, "construction": true});
            skLineSegment(sketch, "E196.4.3", {"start": v(530, 5) * mm, "end": v(539.98, 5) * mm});
            skLineSegment(sketch, "E196.5.0", {"start": v(378.3, 371.23) * mm, "end": v(385.36, 378.29) * mm});
            skLineSegment(sketch, "E196.5.1", {"start": v(378.3, 371.23) * mm, "end": v(371.23, 378.3) * mm});
            skLineSegment(sketch, "E196.5.2", {"start": v(381.84, 381.84) * mm, "end": v(367.7, 367.7) * mm, "construction": true});
            skLineSegment(sketch, "E196.5.3", {"start": v(371.23, 378.3) * mm, "end": v(378.29, 385.36) * mm});
            skLineSegment(sketch, "E196.6.0", {"start": v(5, 530) * mm, "end": v(5, 539.98) * mm});
            skLineSegment(sketch, "E196.6.1", {"start": v(5, 530) * mm, "end": v(-5, 530) * mm});
            skLineSegment(sketch, "E196.6.2", {"start": v(0, 540) * mm, "end": v(0, 520) * mm, "construction": true});
            skLineSegment(sketch, "E196.6.3", {"start": v(-5, 530) * mm, "end": v(-5, 539.98) * mm});
            skLineSegment(sketch, "E196.7.0", {"start": v(-371.23, 378.3) * mm, "end": v(-378.29, 385.36) * mm});
            skLineSegment(sketch, "E196.7.1", {"start": v(-371.23, 378.3) * mm, "end": v(-378.3, 371.23) * mm});
            skLineSegment(sketch, "E196.7.2", {"start": v(-381.84, 381.84) * mm, "end": v(-367.7, 367.7) * mm, "construction": true});
            skLineSegment(sketch, "E196.7.3", {"start": v(-378.3, 371.23) * mm, "end": v(-385.36, 378.29) * mm});
            skArc(sketch, "E197.trimOffspring", {"start": v(-385.36, 378.29) * mm, "mid": v(-498.9, 206.65) * mm, "end": v(-539.98, 5) * mm});
            skArc(sketch, "E198.trimOffspring", {"start": v(-5, 539.98) * mm, "mid": v(-206.65, 498.9) * mm, "end": v(-378.29, 385.36) * mm});
            skArc(sketch, "E199.trimOffspring", {"start": v(378.29, 385.36) * mm, "mid": v(206.65, 498.9) * mm, "end": v(5, 539.98) * mm});
            skArc(sketch, "E200.trimOffspring", {"start": v(539.98, 5) * mm, "mid": v(498.9, 206.65) * mm, "end": v(385.36, 378.29) * mm});
            skArc(sketch, "E201.trimOffspring", {"start": v(385.36, -378.29) * mm, "mid": v(498.9, -206.65) * mm, "end": v(539.98, -5) * mm});
            skArc(sketch, "E202.trimOffspring", {"start": v(5, -539.98) * mm, "mid": v(206.65, -498.9) * mm, "end": v(378.29, -385.36) * mm});
            skArc(sketch, "E203.trimOffspring", {"start": v(-378.29, -385.36) * mm, "mid": v(-206.65, -498.9) * mm, "end": v(-5, -539.98) * mm});
            skSolve(sketch);
        }
        {
            var Q0;
            Q0=qSketchRegion(id+"F13",true);
            extrude(context, id + "F14", {"entities" : qUnion([Q0]), "depth" : 10 * mm, "offsetDistance" : 25 * mm});
        }
        {
            var Q0;
            Q0=qCreatedBy(id+"F3.planeOp",FACE);
            var sketch = newSketch(context, id + "F15", { "sketchPlane" : qUnion([Q0])});
            skPoint(sketch, "E204.0", {"position": v(-280, 0) * mm});
            skPoint(sketch, "E205.0", {"position": v(-290, -5) * mm});
            skPoint(sketch, "E206.0", {"position": v(-290, 5) * mm});
            skPoint(sketch, "E207.0", {"position": v(-300, 0) * mm});
            skArc(sketch, "E208", {"start": v(-299.96, -5) * mm, "mid": v(-277.16, -114.8) * mm, "end": v(-215.64, -208.57) * mm});
            skCircle(sketch, "E209", {"center": v(0, 0) * mm, "radius": 280 * mm});
            skLineSegment(sketch, "E210", {"start": v(-290, 5) * mm, "end": v(-290, -5) * mm});
            skLineSegment(sketch, "E211", {"start": v(-290, -5) * mm, "end": v(-299.96, -5) * mm});
            skLineSegment(sketch, "E212", {"start": v(-290, 5) * mm, "end": v(-299.96, 5) * mm});
            skLineSegment(sketch, "E213.1.0", {"start": v(-208.6, -201.53) * mm, "end": v(-215.64, -208.57) * mm});
            skLineSegment(sketch, "E213.1.1", {"start": v(-208.6, -201.53) * mm, "end": v(-201.53, -208.6) * mm});
            skLineSegment(sketch, "E213.1.2", {"start": v(-201.53, -208.6) * mm, "end": v(-208.57, -215.64) * mm});
            skLineSegment(sketch, "E213.2.0", {"start": v(-5, -290) * mm, "end": v(-5, -299.96) * mm});
            skLineSegment(sketch, "E213.2.1", {"start": v(-5, -290) * mm, "end": v(5, -290) * mm});
            skLineSegment(sketch, "E213.2.2", {"start": v(5, -290) * mm, "end": v(5, -299.96) * mm});
            skLineSegment(sketch, "E213.3.0", {"start": v(201.53, -208.6) * mm, "end": v(208.57, -215.64) * mm});
            skLineSegment(sketch, "E213.3.1", {"start": v(201.53, -208.6) * mm, "end": v(208.6, -201.53) * mm});
            skLineSegment(sketch, "E213.3.2", {"start": v(208.6, -201.53) * mm, "end": v(215.64, -208.57) * mm});
            skLineSegment(sketch, "E213.4.0", {"start": v(290, -5) * mm, "end": v(299.96, -5) * mm});
            skLineSegment(sketch, "E213.4.1", {"start": v(290, -5) * mm, "end": v(290, 5) * mm});
            skLineSegment(sketch, "E213.4.2", {"start": v(290, 5) * mm, "end": v(299.96, 5) * mm});
            skLineSegment(sketch, "E213.5.0", {"start": v(208.6, 201.53) * mm, "end": v(215.64, 208.57) * mm});
            skLineSegment(sketch, "E213.5.1", {"start": v(208.6, 201.53) * mm, "end": v(201.53, 208.6) * mm});
            skLineSegment(sketch, "E213.5.2", {"start": v(201.53, 208.6) * mm, "end": v(208.57, 215.64) * mm});
            skLineSegment(sketch, "E213.6.0", {"start": v(5, 290) * mm, "end": v(5, 299.96) * mm});
            skLineSegment(sketch, "E213.6.1", {"start": v(5, 290) * mm, "end": v(-5, 290) * mm});
            skLineSegment(sketch, "E213.6.2", {"start": v(-5, 290) * mm, "end": v(-5, 299.96) * mm});
            skLineSegment(sketch, "E213.7.0", {"start": v(-201.53, 208.6) * mm, "end": v(-208.57, 215.64) * mm});
            skLineSegment(sketch, "E213.7.1", {"start": v(-201.53, 208.6) * mm, "end": v(-208.6, 201.53) * mm});
            skLineSegment(sketch, "E213.7.2", {"start": v(-208.6, 201.53) * mm, "end": v(-215.64, 208.57) * mm});
            skArc(sketch, "E214.trimOffspring", {"start": v(-215.64, 208.57) * mm, "mid": v(-277.16, 114.8) * mm, "end": v(-299.96, 5) * mm});
            skArc(sketch, "E215.trimOffspring", {"start": v(-5, 299.96) * mm, "mid": v(-114.8, 277.16) * mm, "end": v(-208.57, 215.64) * mm});
            skArc(sketch, "E216.trimOffspring", {"start": v(208.57, 215.64) * mm, "mid": v(114.8, 277.16) * mm, "end": v(5, 299.96) * mm});
            skArc(sketch, "E217.trimOffspring", {"start": v(299.96, 5) * mm, "mid": v(277.16, 114.8) * mm, "end": v(215.64, 208.57) * mm});
            skArc(sketch, "E218.trimOffspring", {"start": v(215.64, -208.57) * mm, "mid": v(277.16, -114.8) * mm, "end": v(299.96, -5) * mm});
            skArc(sketch, "E219.trimOffspring", {"start": v(5, -299.96) * mm, "mid": v(114.8, -277.16) * mm, "end": v(208.57, -215.64) * mm});
            skArc(sketch, "E220.trimOffspring", {"start": v(-208.57, -215.64) * mm, "mid": v(-114.8, -277.16) * mm, "end": v(-5, -299.96) * mm});
            skSolve(sketch);
        }
        {
            var Q0;
            Q0=qSketchRegion(id+"F15",true);
            extrude(context, id + "F16", {"entities" : qUnion([Q0]), "depth" : 10 * mm, "offsetDistance" : 25 * mm});
        }
        {
            var Q0;
            Q0=makeQuery(id+"F11.opExtrude","SWEPT_BODY",BODY,{"disambiguationData":[OSD([sQuery(id+"F10.wireOp",EDGE,"E173"),sQuery(id+"F10.wireOp",EDGE,"E174"),sQuery(id+"F10.wireOp",EDGE,"E175"),sQuery(id+"F10.wireOp",EDGE,"E176"),sQuery(id+"F10.wireOp",EDGE,"E177"),sQuery(id+"F10.wireOp",EDGE,"E178"),sQuery(id+"F10.wireOp",EDGE,"E179"),sQuery(id+"F10.wireOp",EDGE,"E180"),sQuery(id+"F10.wireOp",EDGE,"E181"),sQuery(id+"F10.wireOp",EDGE,"E182"),sQuery(id+"F10.wireOp",EDGE,"E183"),sQuery(id+"F10.wireOp",EDGE,"E184"),sQuery(id+"F10.wireOp",EDGE,"E185.filletArc")])]});
            var Q1;
            Q1=makeQuery(id+"F5.opExtrude","CAP_EDGE",EDGE,{"disambiguationData":[OSD([sQuery(id+"F4.wireOp",EDGE,"E5")])],"isStart":true});
            circularPattern(context, id + "F17", {"operationType" : NewBodyOperationType.ADD, "entities" : qUnion([Q0]), "axis" : qUnion([Q1]), "angle" : 360 * degree, "instanceCount" : 8, "equalSpace" : true});
        }
    });
